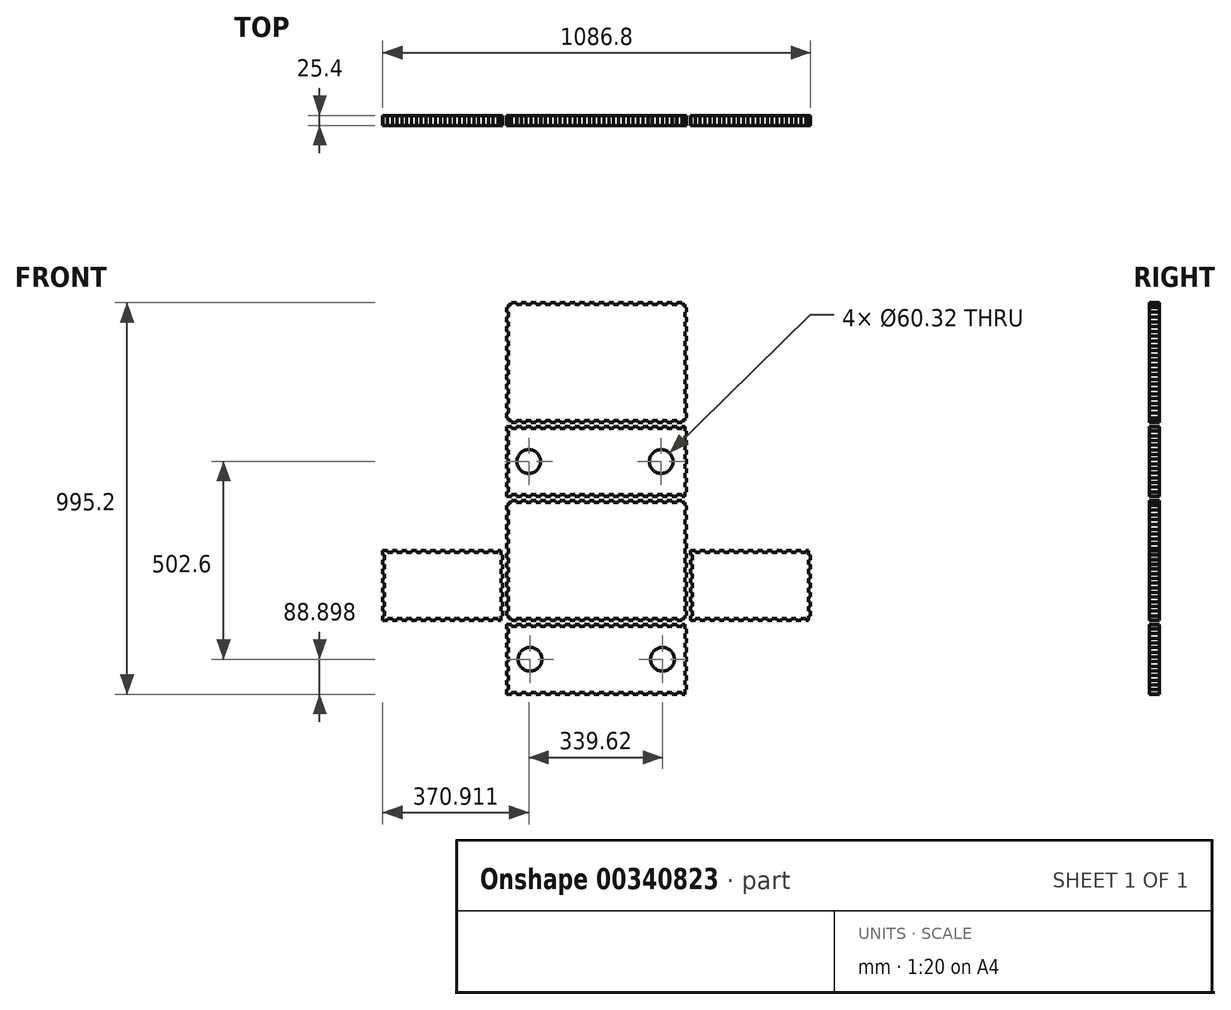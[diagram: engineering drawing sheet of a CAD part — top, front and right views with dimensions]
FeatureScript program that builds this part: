
annotation { "Feature Type Name" : "Feature", "Feature Type Description" : "" }
export const myFeature = defineFeature(function(context is Context, id is Id, definition is map)
    precondition{}
    {
        {
            var Q0;
            Q0=qCreatedBy(makeId("Front.planeOp"),FACE);
            var sketch = newSketch(context, id + "F0", { "sketchPlane" : qUnion([Q0])});
            skLineSegment(sketch, "E0", {"start": v(-228.6, -497.6) * mm, "end": v(-216.24, -497.6) * mm});
            skLineSegment(sketch, "E1", {"start": v(-216.24, -492.84) * mm, "end": v(-216.24, -497.6) * mm});
            skLineSegment(sketch, "E2", {"start": v(-216.24, -492.84) * mm, "end": v(-203.89, -492.84) * mm});
            skLineSegment(sketch, "E3", {"start": v(-203.89, -492.84) * mm, "end": v(-203.89, -497.6) * mm});
            skLineSegment(sketch, "E4", {"start": v(-203.89, -497.6) * mm, "end": v(-191.53, -497.6) * mm});
            skLineSegment(sketch, "E5", {"start": v(-191.53, -492.84) * mm, "end": v(-191.53, -497.6) * mm});
            skLineSegment(sketch, "E6", {"start": v(-191.53, -492.84) * mm, "end": v(-179.17, -492.84) * mm});
            skLineSegment(sketch, "E7", {"start": v(-179.17, -492.84) * mm, "end": v(-179.17, -497.6) * mm});
            skLineSegment(sketch, "E8", {"start": v(-179.17, -497.6) * mm, "end": v(-166.81, -497.6) * mm});
            skLineSegment(sketch, "E9", {"start": v(-166.81, -492.84) * mm, "end": v(-166.81, -497.6) * mm});
            skLineSegment(sketch, "E10", {"start": v(-166.81, -492.84) * mm, "end": v(-154.46, -492.84) * mm});
            skLineSegment(sketch, "E11", {"start": v(-154.46, -492.84) * mm, "end": v(-154.46, -497.6) * mm});
            skLineSegment(sketch, "E12", {"start": v(-154.46, -497.6) * mm, "end": v(-142.1, -497.6) * mm});
            skLineSegment(sketch, "E13", {"start": v(-142.1, -492.84) * mm, "end": v(-142.1, -497.6) * mm});
            skLineSegment(sketch, "E14", {"start": v(-142.1, -492.84) * mm, "end": v(-129.75, -492.84) * mm});
            skLineSegment(sketch, "E15", {"start": v(-129.75, -492.84) * mm, "end": v(-129.75, -497.6) * mm});
            skLineSegment(sketch, "E16", {"start": v(-129.75, -497.6) * mm, "end": v(-117.39, -497.6) * mm});
            skLineSegment(sketch, "E17", {"start": v(-117.39, -492.84) * mm, "end": v(-117.39, -497.6) * mm});
            skLineSegment(sketch, "E18", {"start": v(-117.39, -492.84) * mm, "end": v(-105.03, -492.84) * mm});
            skLineSegment(sketch, "E19", {"start": v(-105.03, -492.84) * mm, "end": v(-105.03, -497.6) * mm});
            skLineSegment(sketch, "E20", {"start": v(-105.03, -497.6) * mm, "end": v(-92.68, -497.6) * mm});
            skLineSegment(sketch, "E21", {"start": v(-92.68, -492.84) * mm, "end": v(-92.68, -497.6) * mm});
            skLineSegment(sketch, "E22", {"start": v(-92.68, -492.84) * mm, "end": v(-80.32, -492.84) * mm});
            skLineSegment(sketch, "E23", {"start": v(-80.32, -492.84) * mm, "end": v(-80.32, -497.6) * mm});
            skLineSegment(sketch, "E24", {"start": v(-80.32, -497.6) * mm, "end": v(-67.96, -497.6) * mm});
            skLineSegment(sketch, "E25", {"start": v(-67.96, -492.84) * mm, "end": v(-67.96, -497.6) * mm});
            skLineSegment(sketch, "E26", {"start": v(-67.96, -492.84) * mm, "end": v(-55.6, -492.84) * mm});
            skLineSegment(sketch, "E27", {"start": v(-55.6, -492.84) * mm, "end": v(-55.6, -497.6) * mm});
            skLineSegment(sketch, "E28", {"start": v(-55.6, -497.6) * mm, "end": v(-43.25, -497.6) * mm});
            skLineSegment(sketch, "E29", {"start": v(-43.25, -492.84) * mm, "end": v(-43.25, -497.6) * mm});
            skLineSegment(sketch, "E30", {"start": v(-43.25, -492.84) * mm, "end": v(-30.89, -492.84) * mm});
            skLineSegment(sketch, "E31", {"start": v(-30.89, -492.84) * mm, "end": v(-30.89, -497.6) * mm});
            skLineSegment(sketch, "E32", {"start": v(-30.89, -497.6) * mm, "end": v(-18.54, -497.6) * mm});
            skLineSegment(sketch, "E33", {"start": v(-18.54, -492.84) * mm, "end": v(-18.54, -497.6) * mm});
            skLineSegment(sketch, "E34", {"start": v(-18.54, -492.84) * mm, "end": v(-6.18, -492.84) * mm});
            skLineSegment(sketch, "E35", {"start": v(-6.18, -492.84) * mm, "end": v(-6.18, -497.6) * mm});
            skLineSegment(sketch, "E36", {"start": v(-6.18, -497.6) * mm, "end": v(6.18, -497.6) * mm});
            skLineSegment(sketch, "E37", {"start": v(6.18, -492.84) * mm, "end": v(6.18, -497.6) * mm});
            skLineSegment(sketch, "E38", {"start": v(6.18, -492.84) * mm, "end": v(18.53, -492.84) * mm});
            skLineSegment(sketch, "E39", {"start": v(18.53, -492.84) * mm, "end": v(18.53, -497.6) * mm});
            skLineSegment(sketch, "E40", {"start": v(18.53, -497.6) * mm, "end": v(30.9, -497.6) * mm});
            skLineSegment(sketch, "E41", {"start": v(30.9, -492.84) * mm, "end": v(30.9, -497.6) * mm});
            skLineSegment(sketch, "E42", {"start": v(30.9, -492.84) * mm, "end": v(43.25, -492.84) * mm});
            skLineSegment(sketch, "E43", {"start": v(43.25, -492.84) * mm, "end": v(43.25, -497.6) * mm});
            skLineSegment(sketch, "E44", {"start": v(43.25, -497.6) * mm, "end": v(55.6, -497.6) * mm});
            skLineSegment(sketch, "E45", {"start": v(55.6, -492.84) * mm, "end": v(55.6, -497.6) * mm});
            skLineSegment(sketch, "E46", {"start": v(55.6, -492.84) * mm, "end": v(67.96, -492.84) * mm});
            skLineSegment(sketch, "E47", {"start": v(67.96, -492.84) * mm, "end": v(67.96, -497.6) * mm});
            skLineSegment(sketch, "E48", {"start": v(67.96, -497.6) * mm, "end": v(80.32, -497.6) * mm});
            skLineSegment(sketch, "E49", {"start": v(80.32, -492.84) * mm, "end": v(80.32, -497.6) * mm});
            skLineSegment(sketch, "E50", {"start": v(80.32, -492.84) * mm, "end": v(92.67, -492.84) * mm});
            skLineSegment(sketch, "E51", {"start": v(92.67, -492.84) * mm, "end": v(92.67, -497.6) * mm});
            skLineSegment(sketch, "E52", {"start": v(92.67, -497.6) * mm, "end": v(105.03, -497.6) * mm});
            skLineSegment(sketch, "E53", {"start": v(105.03, -492.84) * mm, "end": v(105.03, -497.6) * mm});
            skLineSegment(sketch, "E54", {"start": v(105.03, -492.84) * mm, "end": v(117.39, -492.84) * mm});
            skLineSegment(sketch, "E55", {"start": v(117.39, -492.84) * mm, "end": v(117.39, -497.6) * mm});
            skLineSegment(sketch, "E56", {"start": v(117.39, -497.6) * mm, "end": v(129.75, -497.6) * mm});
            skLineSegment(sketch, "E57", {"start": v(129.75, -492.84) * mm, "end": v(129.75, -497.6) * mm});
            skLineSegment(sketch, "E58", {"start": v(129.75, -492.84) * mm, "end": v(142.1, -492.84) * mm});
            skLineSegment(sketch, "E59", {"start": v(142.1, -492.84) * mm, "end": v(142.1, -497.6) * mm});
            skLineSegment(sketch, "E60", {"start": v(142.1, -497.6) * mm, "end": v(154.46, -497.6) * mm});
            skLineSegment(sketch, "E61", {"start": v(154.46, -492.84) * mm, "end": v(154.46, -497.6) * mm});
            skLineSegment(sketch, "E62", {"start": v(154.46, -492.84) * mm, "end": v(166.82, -492.84) * mm});
            skLineSegment(sketch, "E63", {"start": v(166.82, -492.84) * mm, "end": v(166.82, -497.6) * mm});
            skLineSegment(sketch, "E64", {"start": v(166.82, -497.6) * mm, "end": v(179.17, -497.6) * mm});
            skLineSegment(sketch, "E65", {"start": v(179.17, -492.84) * mm, "end": v(179.17, -497.6) * mm});
            skLineSegment(sketch, "E66", {"start": v(179.17, -492.84) * mm, "end": v(191.53, -492.84) * mm});
            skLineSegment(sketch, "E67", {"start": v(191.53, -492.84) * mm, "end": v(191.53, -497.6) * mm});
            skLineSegment(sketch, "E68", {"start": v(191.53, -497.6) * mm, "end": v(203.89, -497.6) * mm});
            skLineSegment(sketch, "E69", {"start": v(203.89, -492.84) * mm, "end": v(203.89, -497.6) * mm});
            skLineSegment(sketch, "E70", {"start": v(203.89, -492.84) * mm, "end": v(216.25, -492.84) * mm});
            skLineSegment(sketch, "E71", {"start": v(216.25, -492.84) * mm, "end": v(216.25, -497.6) * mm});
            skLineSegment(sketch, "E72", {"start": v(216.25, -497.6) * mm, "end": v(223.84, -497.6) * mm});
            skLineSegment(sketch, "E73", {"start": v(-228.6, -319.8) * mm, "end": v(-216.24, -319.8) * mm});
            skLineSegment(sketch, "E74", {"start": v(-216.24, -319.8) * mm, "end": v(-216.24, -324.56) * mm});
            skLineSegment(sketch, "E75", {"start": v(-216.24, -324.56) * mm, "end": v(-203.89, -324.56) * mm});
            skLineSegment(sketch, "E76", {"start": v(-203.89, -319.8) * mm, "end": v(-203.89, -324.56) * mm});
            skLineSegment(sketch, "E77", {"start": v(-203.89, -319.8) * mm, "end": v(-191.53, -319.8) * mm});
            skLineSegment(sketch, "E78", {"start": v(-191.53, -319.8) * mm, "end": v(-191.53, -324.56) * mm});
            skLineSegment(sketch, "E79", {"start": v(-191.53, -324.56) * mm, "end": v(-179.17, -324.56) * mm});
            skLineSegment(sketch, "E80", {"start": v(-179.17, -319.8) * mm, "end": v(-179.17, -324.56) * mm});
            skLineSegment(sketch, "E81", {"start": v(-179.17, -319.8) * mm, "end": v(-166.81, -319.8) * mm});
            skLineSegment(sketch, "E82", {"start": v(-166.81, -319.8) * mm, "end": v(-166.81, -324.56) * mm});
            skLineSegment(sketch, "E83", {"start": v(-166.81, -324.56) * mm, "end": v(-154.46, -324.56) * mm});
            skLineSegment(sketch, "E84", {"start": v(-154.46, -319.8) * mm, "end": v(-154.46, -324.56) * mm});
            skLineSegment(sketch, "E85", {"start": v(-154.46, -319.8) * mm, "end": v(-142.1, -319.8) * mm});
            skLineSegment(sketch, "E86", {"start": v(-142.1, -319.8) * mm, "end": v(-142.1, -324.56) * mm});
            skLineSegment(sketch, "E87", {"start": v(-142.1, -324.56) * mm, "end": v(-129.75, -324.56) * mm});
            skLineSegment(sketch, "E88", {"start": v(-129.75, -319.8) * mm, "end": v(-129.75, -324.56) * mm});
            skLineSegment(sketch, "E89", {"start": v(-129.75, -319.8) * mm, "end": v(-117.39, -319.8) * mm});
            skLineSegment(sketch, "E90", {"start": v(-117.39, -319.8) * mm, "end": v(-117.39, -324.56) * mm});
            skLineSegment(sketch, "E91", {"start": v(-117.39, -324.56) * mm, "end": v(-105.03, -324.56) * mm});
            skLineSegment(sketch, "E92", {"start": v(-105.03, -319.8) * mm, "end": v(-105.03, -324.56) * mm});
            skLineSegment(sketch, "E93", {"start": v(-105.03, -319.8) * mm, "end": v(-92.68, -319.8) * mm});
            skLineSegment(sketch, "E94", {"start": v(-92.68, -319.8) * mm, "end": v(-92.68, -324.56) * mm});
            skLineSegment(sketch, "E95", {"start": v(-92.68, -324.56) * mm, "end": v(-80.32, -324.56) * mm});
            skLineSegment(sketch, "E96", {"start": v(-80.32, -319.8) * mm, "end": v(-80.32, -324.56) * mm});
            skLineSegment(sketch, "E97", {"start": v(-80.32, -319.8) * mm, "end": v(-67.96, -319.8) * mm});
            skLineSegment(sketch, "E98", {"start": v(-67.96, -319.8) * mm, "end": v(-67.96, -324.56) * mm});
            skLineSegment(sketch, "E99", {"start": v(-67.96, -324.56) * mm, "end": v(-55.6, -324.56) * mm});
            skLineSegment(sketch, "E100", {"start": v(-55.6, -319.8) * mm, "end": v(-55.6, -324.56) * mm});
            skLineSegment(sketch, "E101", {"start": v(-55.6, -319.8) * mm, "end": v(-43.25, -319.8) * mm});
            skLineSegment(sketch, "E102", {"start": v(-43.25, -319.8) * mm, "end": v(-43.25, -324.56) * mm});
            skLineSegment(sketch, "E103", {"start": v(-43.25, -324.56) * mm, "end": v(-30.89, -324.56) * mm});
            skLineSegment(sketch, "E104", {"start": v(-30.89, -319.8) * mm, "end": v(-30.89, -324.56) * mm});
            skLineSegment(sketch, "E105", {"start": v(-30.89, -319.8) * mm, "end": v(-18.54, -319.8) * mm});
            skLineSegment(sketch, "E106", {"start": v(-18.54, -319.8) * mm, "end": v(-18.54, -324.56) * mm});
            skLineSegment(sketch, "E107", {"start": v(-18.54, -324.56) * mm, "end": v(-6.18, -324.56) * mm});
            skLineSegment(sketch, "E108", {"start": v(-6.18, -319.8) * mm, "end": v(-6.18, -324.56) * mm});
            skLineSegment(sketch, "E109", {"start": v(-6.18, -319.8) * mm, "end": v(6.18, -319.8) * mm});
            skLineSegment(sketch, "E110", {"start": v(6.18, -319.8) * mm, "end": v(6.18, -324.56) * mm});
            skLineSegment(sketch, "E111", {"start": v(6.18, -324.56) * mm, "end": v(18.53, -324.56) * mm});
            skLineSegment(sketch, "E112", {"start": v(18.53, -319.8) * mm, "end": v(18.53, -324.56) * mm});
            skLineSegment(sketch, "E113", {"start": v(18.53, -319.8) * mm, "end": v(30.9, -319.8) * mm});
            skLineSegment(sketch, "E114", {"start": v(30.9, -319.8) * mm, "end": v(30.9, -324.56) * mm});
            skLineSegment(sketch, "E115", {"start": v(30.9, -324.56) * mm, "end": v(43.25, -324.56) * mm});
            skLineSegment(sketch, "E116", {"start": v(43.25, -319.8) * mm, "end": v(43.25, -324.56) * mm});
            skLineSegment(sketch, "E117", {"start": v(43.25, -319.8) * mm, "end": v(55.6, -319.8) * mm});
            skLineSegment(sketch, "E118", {"start": v(55.6, -319.8) * mm, "end": v(55.6, -324.56) * mm});
            skLineSegment(sketch, "E119", {"start": v(55.6, -324.56) * mm, "end": v(67.96, -324.56) * mm});
            skLineSegment(sketch, "E120", {"start": v(67.96, -319.8) * mm, "end": v(67.96, -324.56) * mm});
            skLineSegment(sketch, "E121", {"start": v(67.96, -319.8) * mm, "end": v(80.32, -319.8) * mm});
            skLineSegment(sketch, "E122", {"start": v(80.32, -319.8) * mm, "end": v(80.32, -324.56) * mm});
            skLineSegment(sketch, "E123", {"start": v(80.32, -324.56) * mm, "end": v(92.67, -324.56) * mm});
            skLineSegment(sketch, "E124", {"start": v(92.67, -319.8) * mm, "end": v(92.67, -324.56) * mm});
            skLineSegment(sketch, "E125", {"start": v(92.67, -319.8) * mm, "end": v(105.03, -319.8) * mm});
            skLineSegment(sketch, "E126", {"start": v(105.03, -319.8) * mm, "end": v(105.03, -324.56) * mm});
            skLineSegment(sketch, "E127", {"start": v(105.03, -324.56) * mm, "end": v(117.39, -324.56) * mm});
            skLineSegment(sketch, "E128", {"start": v(117.39, -319.8) * mm, "end": v(117.39, -324.56) * mm});
            skLineSegment(sketch, "E129", {"start": v(117.39, -319.8) * mm, "end": v(129.75, -319.8) * mm});
            skLineSegment(sketch, "E130", {"start": v(129.75, -319.8) * mm, "end": v(129.75, -324.56) * mm});
            skLineSegment(sketch, "E131", {"start": v(129.75, -324.56) * mm, "end": v(142.1, -324.56) * mm});
            skLineSegment(sketch, "E132", {"start": v(142.1, -319.8) * mm, "end": v(142.1, -324.56) * mm});
            skLineSegment(sketch, "E133", {"start": v(142.1, -319.8) * mm, "end": v(154.46, -319.8) * mm});
            skLineSegment(sketch, "E134", {"start": v(154.46, -319.8) * mm, "end": v(154.46, -324.56) * mm});
            skLineSegment(sketch, "E135", {"start": v(154.46, -324.56) * mm, "end": v(166.82, -324.56) * mm});
            skLineSegment(sketch, "E136", {"start": v(166.82, -319.8) * mm, "end": v(166.82, -324.56) * mm});
            skLineSegment(sketch, "E137", {"start": v(166.82, -319.8) * mm, "end": v(179.17, -319.8) * mm});
            skLineSegment(sketch, "E138", {"start": v(179.17, -319.8) * mm, "end": v(179.17, -324.56) * mm});
            skLineSegment(sketch, "E139", {"start": v(179.17, -324.56) * mm, "end": v(191.53, -324.56) * mm});
            skLineSegment(sketch, "E140", {"start": v(191.53, -319.8) * mm, "end": v(191.53, -324.56) * mm});
            skLineSegment(sketch, "E141", {"start": v(191.53, -319.8) * mm, "end": v(203.89, -319.8) * mm});
            skLineSegment(sketch, "E142", {"start": v(203.89, -319.8) * mm, "end": v(203.89, -324.56) * mm});
            skLineSegment(sketch, "E143", {"start": v(203.89, -324.56) * mm, "end": v(216.25, -324.56) * mm});
            skLineSegment(sketch, "E144", {"start": v(216.25, -319.8) * mm, "end": v(216.25, -324.56) * mm});
            skLineSegment(sketch, "E145", {"start": v(216.25, -319.8) * mm, "end": v(223.84, -319.8) * mm});
            skLineSegment(sketch, "E146", {"start": v(-228.6, -497.6) * mm, "end": v(-228.6, -485.75) * mm});
            skLineSegment(sketch, "E147", {"start": v(-223.84, -485.75) * mm, "end": v(-228.6, -485.75) * mm});
            skLineSegment(sketch, "E148", {"start": v(-223.84, -485.75) * mm, "end": v(-223.84, -473.9) * mm});
            skLineSegment(sketch, "E149", {"start": v(-223.84, -473.9) * mm, "end": v(-228.6, -473.9) * mm});
            skLineSegment(sketch, "E150", {"start": v(-228.6, -473.9) * mm, "end": v(-228.6, -462.04) * mm});
            skLineSegment(sketch, "E151", {"start": v(-223.84, -462.04) * mm, "end": v(-228.6, -462.04) * mm});
            skLineSegment(sketch, "E152", {"start": v(-223.84, -462.04) * mm, "end": v(-223.84, -450.19) * mm});
            skLineSegment(sketch, "E153", {"start": v(-223.84, -450.19) * mm, "end": v(-228.6, -450.19) * mm});
            skLineSegment(sketch, "E154", {"start": v(-228.6, -450.19) * mm, "end": v(-228.6, -438.33) * mm});
            skLineSegment(sketch, "E155", {"start": v(-223.84, -438.33) * mm, "end": v(-228.6, -438.33) * mm});
            skLineSegment(sketch, "E156", {"start": v(-223.84, -438.33) * mm, "end": v(-223.84, -426.48) * mm});
            skLineSegment(sketch, "E157", {"start": v(-223.84, -426.48) * mm, "end": v(-228.6, -426.48) * mm});
            skLineSegment(sketch, "E158", {"start": v(-228.6, -426.48) * mm, "end": v(-228.6, -414.63) * mm});
            skLineSegment(sketch, "E159", {"start": v(-223.84, -414.63) * mm, "end": v(-228.6, -414.63) * mm});
            skLineSegment(sketch, "E160", {"start": v(-223.84, -414.63) * mm, "end": v(-223.84, -402.78) * mm});
            skLineSegment(sketch, "E161", {"start": v(-223.84, -402.78) * mm, "end": v(-228.6, -402.78) * mm});
            skLineSegment(sketch, "E162", {"start": v(-228.6, -402.78) * mm, "end": v(-228.6, -390.92) * mm});
            skLineSegment(sketch, "E163", {"start": v(-223.84, -390.92) * mm, "end": v(-228.6, -390.92) * mm});
            skLineSegment(sketch, "E164", {"start": v(-223.84, -390.92) * mm, "end": v(-223.84, -379.07) * mm});
            skLineSegment(sketch, "E165", {"start": v(-223.84, -379.07) * mm, "end": v(-228.6, -379.07) * mm});
            skLineSegment(sketch, "E166", {"start": v(-228.6, -379.07) * mm, "end": v(-228.6, -367.22) * mm});
            skLineSegment(sketch, "E167", {"start": v(-223.84, -367.22) * mm, "end": v(-228.6, -367.22) * mm});
            skLineSegment(sketch, "E168", {"start": v(-223.84, -367.22) * mm, "end": v(-223.84, -355.36) * mm});
            skLineSegment(sketch, "E169", {"start": v(-223.84, -355.36) * mm, "end": v(-228.6, -355.36) * mm});
            skLineSegment(sketch, "E170", {"start": v(-228.6, -355.36) * mm, "end": v(-228.6, -343.5) * mm});
            skLineSegment(sketch, "E171", {"start": v(-223.84, -343.5) * mm, "end": v(-228.6, -343.5) * mm});
            skLineSegment(sketch, "E172", {"start": v(-223.84, -343.5) * mm, "end": v(-223.84, -331.65) * mm});
            skLineSegment(sketch, "E173", {"start": v(-223.84, -331.65) * mm, "end": v(-228.6, -331.65) * mm});
            skLineSegment(sketch, "E174", {"start": v(-228.6, -331.65) * mm, "end": v(-228.6, -319.8) * mm});
            skLineSegment(sketch, "E175", {"start": v(223.84, -497.6) * mm, "end": v(223.84, -485.75) * mm});
            skLineSegment(sketch, "E176", {"start": v(228.6, -485.75) * mm, "end": v(223.84, -485.75) * mm});
            skLineSegment(sketch, "E177", {"start": v(228.6, -485.75) * mm, "end": v(228.6, -473.9) * mm});
            skLineSegment(sketch, "E178", {"start": v(228.6, -473.9) * mm, "end": v(223.84, -473.9) * mm});
            skLineSegment(sketch, "E179", {"start": v(223.84, -473.9) * mm, "end": v(223.84, -462.04) * mm});
            skLineSegment(sketch, "E180", {"start": v(228.6, -462.04) * mm, "end": v(223.84, -462.04) * mm});
            skLineSegment(sketch, "E181", {"start": v(228.6, -462.04) * mm, "end": v(228.6, -450.19) * mm});
            skLineSegment(sketch, "E182", {"start": v(228.6, -450.19) * mm, "end": v(223.84, -450.19) * mm});
            skLineSegment(sketch, "E183", {"start": v(223.84, -450.19) * mm, "end": v(223.84, -438.33) * mm});
            skLineSegment(sketch, "E184", {"start": v(228.6, -438.33) * mm, "end": v(223.84, -438.33) * mm});
            skLineSegment(sketch, "E185", {"start": v(228.6, -438.33) * mm, "end": v(228.6, -426.48) * mm});
            skLineSegment(sketch, "E186", {"start": v(228.6, -426.48) * mm, "end": v(223.84, -426.48) * mm});
            skLineSegment(sketch, "E187", {"start": v(223.84, -426.48) * mm, "end": v(223.84, -414.63) * mm});
            skLineSegment(sketch, "E188", {"start": v(228.6, -414.63) * mm, "end": v(223.84, -414.63) * mm});
            skLineSegment(sketch, "E189", {"start": v(228.6, -414.63) * mm, "end": v(228.6, -402.78) * mm});
            skLineSegment(sketch, "E190", {"start": v(228.6, -402.78) * mm, "end": v(223.84, -402.78) * mm});
            skLineSegment(sketch, "E191", {"start": v(223.84, -402.78) * mm, "end": v(223.84, -390.92) * mm});
            skLineSegment(sketch, "E192", {"start": v(228.6, -390.92) * mm, "end": v(223.84, -390.92) * mm});
            skLineSegment(sketch, "E193", {"start": v(228.6, -390.92) * mm, "end": v(228.6, -379.07) * mm});
            skLineSegment(sketch, "E194", {"start": v(228.6, -379.07) * mm, "end": v(223.84, -379.07) * mm});
            skLineSegment(sketch, "E195", {"start": v(223.84, -379.07) * mm, "end": v(223.84, -367.22) * mm});
            skLineSegment(sketch, "E196", {"start": v(228.6, -367.22) * mm, "end": v(223.84, -367.22) * mm});
            skLineSegment(sketch, "E197", {"start": v(228.6, -367.22) * mm, "end": v(228.6, -355.36) * mm});
            skLineSegment(sketch, "E198", {"start": v(228.6, -355.36) * mm, "end": v(223.84, -355.36) * mm});
            skLineSegment(sketch, "E199", {"start": v(223.84, -355.36) * mm, "end": v(223.84, -343.5) * mm});
            skLineSegment(sketch, "E200", {"start": v(228.6, -343.5) * mm, "end": v(223.84, -343.5) * mm});
            skLineSegment(sketch, "E201", {"start": v(228.6, -343.5) * mm, "end": v(228.6, -331.65) * mm});
            skLineSegment(sketch, "E202", {"start": v(228.6, -331.65) * mm, "end": v(223.84, -331.65) * mm});
            skLineSegment(sketch, "E203", {"start": v(223.84, -331.65) * mm, "end": v(223.84, -319.8) * mm});
            skLineSegment(sketch, "E204", {"start": v(-543.4, -309.8) * mm, "end": v(-531.2, -309.8) * mm});
            skLineSegment(sketch, "E205", {"start": v(-531.2, -305.04) * mm, "end": v(-531.2, -309.8) * mm});
            skLineSegment(sketch, "E206", {"start": v(-531.2, -305.04) * mm, "end": v(-519.02, -305.04) * mm});
            skLineSegment(sketch, "E207", {"start": v(-519.02, -305.04) * mm, "end": v(-519.02, -309.8) * mm});
            skLineSegment(sketch, "E208", {"start": v(-519.02, -309.8) * mm, "end": v(-506.82, -309.8) * mm});
            skLineSegment(sketch, "E209", {"start": v(-506.82, -305.04) * mm, "end": v(-506.82, -309.8) * mm});
            skLineSegment(sketch, "E210", {"start": v(-506.82, -305.04) * mm, "end": v(-494.63, -305.04) * mm});
            skLineSegment(sketch, "E211", {"start": v(-494.63, -305.04) * mm, "end": v(-494.63, -309.8) * mm});
            skLineSegment(sketch, "E212", {"start": v(-494.63, -309.8) * mm, "end": v(-482.44, -309.8) * mm});
            skLineSegment(sketch, "E213", {"start": v(-482.44, -305.04) * mm, "end": v(-482.44, -309.8) * mm});
            skLineSegment(sketch, "E214", {"start": v(-482.44, -305.04) * mm, "end": v(-470.25, -305.04) * mm});
            skLineSegment(sketch, "E215", {"start": v(-470.25, -305.04) * mm, "end": v(-470.25, -309.8) * mm});
            skLineSegment(sketch, "E216", {"start": v(-470.25, -309.8) * mm, "end": v(-458.06, -309.8) * mm});
            skLineSegment(sketch, "E217", {"start": v(-458.06, -305.04) * mm, "end": v(-458.06, -309.8) * mm});
            skLineSegment(sketch, "E218", {"start": v(-458.06, -305.04) * mm, "end": v(-445.86, -305.04) * mm});
            skLineSegment(sketch, "E219", {"start": v(-445.86, -305.04) * mm, "end": v(-445.86, -309.8) * mm});
            skLineSegment(sketch, "E220", {"start": v(-445.86, -309.8) * mm, "end": v(-433.67, -309.8) * mm});
            skLineSegment(sketch, "E221", {"start": v(-433.67, -305.04) * mm, "end": v(-433.67, -309.8) * mm});
            skLineSegment(sketch, "E222", {"start": v(-433.67, -305.04) * mm, "end": v(-421.48, -305.04) * mm});
            skLineSegment(sketch, "E223", {"start": v(-421.48, -305.04) * mm, "end": v(-421.48, -309.8) * mm});
            skLineSegment(sketch, "E224", {"start": v(-421.48, -309.8) * mm, "end": v(-409.29, -309.8) * mm});
            skLineSegment(sketch, "E225", {"start": v(-409.29, -305.04) * mm, "end": v(-409.29, -309.8) * mm});
            skLineSegment(sketch, "E226", {"start": v(-409.29, -305.04) * mm, "end": v(-397.1, -305.04) * mm});
            skLineSegment(sketch, "E227", {"start": v(-397.1, -305.04) * mm, "end": v(-397.1, -309.8) * mm});
            skLineSegment(sketch, "E228", {"start": v(-397.1, -309.8) * mm, "end": v(-384.9, -309.8) * mm});
            skLineSegment(sketch, "E229", {"start": v(-384.9, -305.04) * mm, "end": v(-384.9, -309.8) * mm});
            skLineSegment(sketch, "E230", {"start": v(-384.9, -305.04) * mm, "end": v(-372.71, -305.04) * mm});
            skLineSegment(sketch, "E231", {"start": v(-372.71, -305.04) * mm, "end": v(-372.71, -309.8) * mm});
            skLineSegment(sketch, "E232", {"start": v(-372.71, -309.8) * mm, "end": v(-360.52, -309.8) * mm});
            skLineSegment(sketch, "E233", {"start": v(-360.52, -305.04) * mm, "end": v(-360.52, -309.8) * mm});
            skLineSegment(sketch, "E234", {"start": v(-360.52, -305.04) * mm, "end": v(-348.33, -305.04) * mm});
            skLineSegment(sketch, "E235", {"start": v(-348.33, -305.04) * mm, "end": v(-348.33, -309.8) * mm});
            skLineSegment(sketch, "E236", {"start": v(-348.33, -309.8) * mm, "end": v(-336.14, -309.8) * mm});
            skLineSegment(sketch, "E237", {"start": v(-336.14, -305.04) * mm, "end": v(-336.14, -309.8) * mm});
            skLineSegment(sketch, "E238", {"start": v(-336.14, -305.04) * mm, "end": v(-323.94, -305.04) * mm});
            skLineSegment(sketch, "E239", {"start": v(-323.94, -305.04) * mm, "end": v(-323.94, -309.8) * mm});
            skLineSegment(sketch, "E240", {"start": v(-323.94, -309.8) * mm, "end": v(-311.75, -309.8) * mm});
            skLineSegment(sketch, "E241", {"start": v(-311.75, -305.04) * mm, "end": v(-311.75, -309.8) * mm});
            skLineSegment(sketch, "E242", {"start": v(-311.75, -305.04) * mm, "end": v(-299.56, -305.04) * mm});
            skLineSegment(sketch, "E243", {"start": v(-299.56, -305.04) * mm, "end": v(-299.56, -309.8) * mm});
            skLineSegment(sketch, "E244", {"start": v(-299.56, -309.8) * mm, "end": v(-287.37, -309.8) * mm});
            skLineSegment(sketch, "E245", {"start": v(-287.37, -305.04) * mm, "end": v(-287.37, -309.8) * mm});
            skLineSegment(sketch, "E246", {"start": v(-287.37, -305.04) * mm, "end": v(-275.18, -305.04) * mm});
            skLineSegment(sketch, "E247", {"start": v(-275.18, -305.04) * mm, "end": v(-275.18, -309.8) * mm});
            skLineSegment(sketch, "E248", {"start": v(-275.18, -309.8) * mm, "end": v(-262.98, -309.8) * mm});
            skLineSegment(sketch, "E249", {"start": v(-262.98, -305.04) * mm, "end": v(-262.98, -309.8) * mm});
            skLineSegment(sketch, "E250", {"start": v(-262.98, -305.04) * mm, "end": v(-250.8, -305.04) * mm});
            skLineSegment(sketch, "E251", {"start": v(-250.8, -305.04) * mm, "end": v(-250.8, -309.8) * mm});
            skLineSegment(sketch, "E252", {"start": v(-250.8, -309.8) * mm, "end": v(-243.36, -309.8) * mm});
            skLineSegment(sketch, "E253", {"start": v(-543.4, -132) * mm, "end": v(-531.2, -132) * mm});
            skLineSegment(sketch, "E254", {"start": v(-531.2, -132) * mm, "end": v(-531.2, -136.76) * mm});
            skLineSegment(sketch, "E255", {"start": v(-531.2, -136.76) * mm, "end": v(-519.02, -136.76) * mm});
            skLineSegment(sketch, "E256", {"start": v(-519.02, -132) * mm, "end": v(-519.02, -136.76) * mm});
            skLineSegment(sketch, "E257", {"start": v(-519.02, -132) * mm, "end": v(-506.82, -132) * mm});
            skLineSegment(sketch, "E258", {"start": v(-506.82, -132) * mm, "end": v(-506.82, -136.76) * mm});
            skLineSegment(sketch, "E259", {"start": v(-506.82, -136.76) * mm, "end": v(-494.63, -136.76) * mm});
            skLineSegment(sketch, "E260", {"start": v(-494.63, -132) * mm, "end": v(-494.63, -136.76) * mm});
            skLineSegment(sketch, "E261", {"start": v(-494.63, -132) * mm, "end": v(-482.44, -132) * mm});
            skLineSegment(sketch, "E262", {"start": v(-482.44, -132) * mm, "end": v(-482.44, -136.76) * mm});
            skLineSegment(sketch, "E263", {"start": v(-482.44, -136.76) * mm, "end": v(-470.25, -136.76) * mm});
            skLineSegment(sketch, "E264", {"start": v(-470.25, -132) * mm, "end": v(-470.25, -136.76) * mm});
            skLineSegment(sketch, "E265", {"start": v(-470.25, -132) * mm, "end": v(-458.06, -132) * mm});
            skLineSegment(sketch, "E266", {"start": v(-458.06, -132) * mm, "end": v(-458.06, -136.76) * mm});
            skLineSegment(sketch, "E267", {"start": v(-458.06, -136.76) * mm, "end": v(-445.86, -136.76) * mm});
            skLineSegment(sketch, "E268", {"start": v(-445.86, -132) * mm, "end": v(-445.86, -136.76) * mm});
            skLineSegment(sketch, "E269", {"start": v(-445.86, -132) * mm, "end": v(-433.67, -132) * mm});
            skLineSegment(sketch, "E270", {"start": v(-433.67, -132) * mm, "end": v(-433.67, -136.76) * mm});
            skLineSegment(sketch, "E271", {"start": v(-433.67, -136.76) * mm, "end": v(-421.48, -136.76) * mm});
            skLineSegment(sketch, "E272", {"start": v(-421.48, -132) * mm, "end": v(-421.48, -136.76) * mm});
            skLineSegment(sketch, "E273", {"start": v(-421.48, -132) * mm, "end": v(-409.29, -132) * mm});
            skLineSegment(sketch, "E274", {"start": v(-409.29, -132) * mm, "end": v(-409.29, -136.76) * mm});
            skLineSegment(sketch, "E275", {"start": v(-409.29, -136.76) * mm, "end": v(-397.1, -136.76) * mm});
            skLineSegment(sketch, "E276", {"start": v(-397.1, -132) * mm, "end": v(-397.1, -136.76) * mm});
            skLineSegment(sketch, "E277", {"start": v(-397.1, -132) * mm, "end": v(-384.9, -132) * mm});
            skLineSegment(sketch, "E278", {"start": v(-384.9, -132) * mm, "end": v(-384.9, -136.76) * mm});
            skLineSegment(sketch, "E279", {"start": v(-384.9, -136.76) * mm, "end": v(-372.71, -136.76) * mm});
            skLineSegment(sketch, "E280", {"start": v(-372.71, -132) * mm, "end": v(-372.71, -136.76) * mm});
            skLineSegment(sketch, "E281", {"start": v(-372.71, -132) * mm, "end": v(-360.52, -132) * mm});
            skLineSegment(sketch, "E282", {"start": v(-360.52, -132) * mm, "end": v(-360.52, -136.76) * mm});
            skLineSegment(sketch, "E283", {"start": v(-360.52, -136.76) * mm, "end": v(-348.33, -136.76) * mm});
            skLineSegment(sketch, "E284", {"start": v(-348.33, -132) * mm, "end": v(-348.33, -136.76) * mm});
            skLineSegment(sketch, "E285", {"start": v(-348.33, -132) * mm, "end": v(-336.14, -132) * mm});
            skLineSegment(sketch, "E286", {"start": v(-336.14, -132) * mm, "end": v(-336.14, -136.76) * mm});
            skLineSegment(sketch, "E287", {"start": v(-336.14, -136.76) * mm, "end": v(-323.94, -136.76) * mm});
            skLineSegment(sketch, "E288", {"start": v(-323.94, -132) * mm, "end": v(-323.94, -136.76) * mm});
            skLineSegment(sketch, "E289", {"start": v(-323.94, -132) * mm, "end": v(-311.75, -132) * mm});
            skLineSegment(sketch, "E290", {"start": v(-311.75, -132) * mm, "end": v(-311.75, -136.76) * mm});
            skLineSegment(sketch, "E291", {"start": v(-311.75, -136.76) * mm, "end": v(-299.56, -136.76) * mm});
            skLineSegment(sketch, "E292", {"start": v(-299.56, -132) * mm, "end": v(-299.56, -136.76) * mm});
            skLineSegment(sketch, "E293", {"start": v(-299.56, -132) * mm, "end": v(-287.37, -132) * mm});
            skLineSegment(sketch, "E294", {"start": v(-287.37, -132) * mm, "end": v(-287.37, -136.76) * mm});
            skLineSegment(sketch, "E295", {"start": v(-287.37, -136.76) * mm, "end": v(-275.18, -136.76) * mm});
            skLineSegment(sketch, "E296", {"start": v(-275.18, -132) * mm, "end": v(-275.18, -136.76) * mm});
            skLineSegment(sketch, "E297", {"start": v(-275.18, -132) * mm, "end": v(-262.98, -132) * mm});
            skLineSegment(sketch, "E298", {"start": v(-262.98, -132) * mm, "end": v(-262.98, -136.76) * mm});
            skLineSegment(sketch, "E299", {"start": v(-262.98, -136.76) * mm, "end": v(-250.8, -136.76) * mm});
            skLineSegment(sketch, "E300", {"start": v(-250.8, -132) * mm, "end": v(-250.8, -136.76) * mm});
            skLineSegment(sketch, "E301", {"start": v(-250.8, -132) * mm, "end": v(-243.36, -132) * mm});
            skLineSegment(sketch, "E302", {"start": v(-543.4, -309.8) * mm, "end": v(-543.4, -297.95) * mm});
            skLineSegment(sketch, "E303", {"start": v(-538.64, -297.95) * mm, "end": v(-543.4, -297.95) * mm});
            skLineSegment(sketch, "E304", {"start": v(-538.64, -297.95) * mm, "end": v(-538.64, -286.1) * mm});
            skLineSegment(sketch, "E305", {"start": v(-538.64, -286.1) * mm, "end": v(-543.4, -286.1) * mm});
            skLineSegment(sketch, "E306", {"start": v(-543.4, -286.1) * mm, "end": v(-543.4, -274.24) * mm});
            skLineSegment(sketch, "E307", {"start": v(-538.64, -274.24) * mm, "end": v(-543.4, -274.24) * mm});
            skLineSegment(sketch, "E308", {"start": v(-538.64, -274.24) * mm, "end": v(-538.64, -262.39) * mm});
            skLineSegment(sketch, "E309", {"start": v(-538.64, -262.39) * mm, "end": v(-543.4, -262.39) * mm});
            skLineSegment(sketch, "E310", {"start": v(-543.4, -262.39) * mm, "end": v(-543.4, -250.54) * mm});
            skLineSegment(sketch, "E311", {"start": v(-538.64, -250.54) * mm, "end": v(-543.4, -250.54) * mm});
            skLineSegment(sketch, "E312", {"start": v(-538.64, -250.54) * mm, "end": v(-538.64, -238.68) * mm});
            skLineSegment(sketch, "E313", {"start": v(-538.64, -238.68) * mm, "end": v(-543.4, -238.68) * mm});
            skLineSegment(sketch, "E314", {"start": v(-543.4, -238.68) * mm, "end": v(-543.4, -226.83) * mm});
            skLineSegment(sketch, "E315", {"start": v(-538.64, -226.83) * mm, "end": v(-543.4, -226.83) * mm});
            skLineSegment(sketch, "E316", {"start": v(-538.64, -226.83) * mm, "end": v(-538.64, -214.98) * mm});
            skLineSegment(sketch, "E317", {"start": v(-538.64, -214.98) * mm, "end": v(-543.4, -214.98) * mm});
            skLineSegment(sketch, "E318", {"start": v(-543.4, -214.98) * mm, "end": v(-543.4, -203.12) * mm});
            skLineSegment(sketch, "E319", {"start": v(-538.64, -203.12) * mm, "end": v(-543.4, -203.12) * mm});
            skLineSegment(sketch, "E320", {"start": v(-538.64, -203.12) * mm, "end": v(-538.64, -191.27) * mm});
            skLineSegment(sketch, "E321", {"start": v(-538.64, -191.27) * mm, "end": v(-543.4, -191.27) * mm});
            skLineSegment(sketch, "E322", {"start": v(-543.4, -191.27) * mm, "end": v(-543.4, -179.42) * mm});
            skLineSegment(sketch, "E323", {"start": v(-538.64, -179.42) * mm, "end": v(-543.4, -179.42) * mm});
            skLineSegment(sketch, "E324", {"start": v(-538.64, -179.42) * mm, "end": v(-538.64, -167.56) * mm});
            skLineSegment(sketch, "E325", {"start": v(-538.64, -167.56) * mm, "end": v(-543.4, -167.56) * mm});
            skLineSegment(sketch, "E326", {"start": v(-543.4, -167.56) * mm, "end": v(-543.4, -155.7) * mm});
            skLineSegment(sketch, "E327", {"start": v(-538.64, -155.7) * mm, "end": v(-543.4, -155.7) * mm});
            skLineSegment(sketch, "E328", {"start": v(-538.64, -155.7) * mm, "end": v(-538.64, -143.86) * mm});
            skLineSegment(sketch, "E329", {"start": v(-538.64, -143.86) * mm, "end": v(-543.4, -143.86) * mm});
            skLineSegment(sketch, "E330", {"start": v(-543.4, -143.86) * mm, "end": v(-543.4, -132) * mm});
            skLineSegment(sketch, "E331", {"start": v(-243.36, -309.8) * mm, "end": v(-243.36, -297.95) * mm});
            skLineSegment(sketch, "E332", {"start": v(-238.6, -297.95) * mm, "end": v(-243.36, -297.95) * mm});
            skLineSegment(sketch, "E333", {"start": v(-238.6, -297.95) * mm, "end": v(-238.6, -286.1) * mm});
            skLineSegment(sketch, "E334", {"start": v(-238.6, -286.1) * mm, "end": v(-243.36, -286.1) * mm});
            skLineSegment(sketch, "E335", {"start": v(-243.36, -286.1) * mm, "end": v(-243.36, -274.24) * mm});
            skLineSegment(sketch, "E336", {"start": v(-238.6, -274.24) * mm, "end": v(-243.36, -274.24) * mm});
            skLineSegment(sketch, "E337", {"start": v(-238.6, -274.24) * mm, "end": v(-238.6, -262.39) * mm});
            skLineSegment(sketch, "E338", {"start": v(-238.6, -262.39) * mm, "end": v(-243.36, -262.39) * mm});
            skLineSegment(sketch, "E339", {"start": v(-243.36, -262.39) * mm, "end": v(-243.36, -250.54) * mm});
            skLineSegment(sketch, "E340", {"start": v(-238.6, -250.54) * mm, "end": v(-243.36, -250.54) * mm});
            skLineSegment(sketch, "E341", {"start": v(-238.6, -250.54) * mm, "end": v(-238.6, -238.68) * mm});
            skLineSegment(sketch, "E342", {"start": v(-238.6, -238.68) * mm, "end": v(-243.36, -238.68) * mm});
            skLineSegment(sketch, "E343", {"start": v(-243.36, -238.68) * mm, "end": v(-243.36, -226.83) * mm});
            skLineSegment(sketch, "E344", {"start": v(-238.6, -226.83) * mm, "end": v(-243.36, -226.83) * mm});
            skLineSegment(sketch, "E345", {"start": v(-238.6, -226.83) * mm, "end": v(-238.6, -214.98) * mm});
            skLineSegment(sketch, "E346", {"start": v(-238.6, -214.98) * mm, "end": v(-243.36, -214.98) * mm});
            skLineSegment(sketch, "E347", {"start": v(-243.36, -214.98) * mm, "end": v(-243.36, -203.12) * mm});
            skLineSegment(sketch, "E348", {"start": v(-238.6, -203.12) * mm, "end": v(-243.36, -203.12) * mm});
            skLineSegment(sketch, "E349", {"start": v(-238.6, -203.12) * mm, "end": v(-238.6, -191.27) * mm});
            skLineSegment(sketch, "E350", {"start": v(-238.6, -191.27) * mm, "end": v(-243.36, -191.27) * mm});
            skLineSegment(sketch, "E351", {"start": v(-243.36, -191.27) * mm, "end": v(-243.36, -179.42) * mm});
            skLineSegment(sketch, "E352", {"start": v(-238.6, -179.42) * mm, "end": v(-243.36, -179.42) * mm});
            skLineSegment(sketch, "E353", {"start": v(-238.6, -179.42) * mm, "end": v(-238.6, -167.56) * mm});
            skLineSegment(sketch, "E354", {"start": v(-238.6, -167.56) * mm, "end": v(-243.36, -167.56) * mm});
            skLineSegment(sketch, "E355", {"start": v(-243.36, -167.56) * mm, "end": v(-243.36, -155.7) * mm});
            skLineSegment(sketch, "E356", {"start": v(-238.6, -155.7) * mm, "end": v(-243.36, -155.7) * mm});
            skLineSegment(sketch, "E357", {"start": v(-238.6, -155.7) * mm, "end": v(-238.6, -143.86) * mm});
            skLineSegment(sketch, "E358", {"start": v(-238.6, -143.86) * mm, "end": v(-243.36, -143.86) * mm});
            skLineSegment(sketch, "E359", {"start": v(-243.36, -143.86) * mm, "end": v(-243.36, -132) * mm});
            skLineSegment(sketch, "E360", {"start": v(-223.84, -305.04) * mm, "end": v(-216.24, -305.04) * mm});
            skLineSegment(sketch, "E361", {"start": v(-216.24, -305.04) * mm, "end": v(-216.24, -309.8) * mm});
            skLineSegment(sketch, "E362", {"start": v(-216.24, -309.8) * mm, "end": v(-203.89, -309.8) * mm});
            skLineSegment(sketch, "E363", {"start": v(-203.89, -305.04) * mm, "end": v(-203.89, -309.8) * mm});
            skLineSegment(sketch, "E364", {"start": v(-203.89, -305.04) * mm, "end": v(-191.53, -305.04) * mm});
            skLineSegment(sketch, "E365", {"start": v(-191.53, -305.04) * mm, "end": v(-191.53, -309.8) * mm});
            skLineSegment(sketch, "E366", {"start": v(-191.53, -309.8) * mm, "end": v(-179.17, -309.8) * mm});
            skLineSegment(sketch, "E367", {"start": v(-179.17, -305.04) * mm, "end": v(-179.17, -309.8) * mm});
            skLineSegment(sketch, "E368", {"start": v(-179.17, -305.04) * mm, "end": v(-166.81, -305.04) * mm});
            skLineSegment(sketch, "E369", {"start": v(-166.81, -305.04) * mm, "end": v(-166.81, -309.8) * mm});
            skLineSegment(sketch, "E370", {"start": v(-166.81, -309.8) * mm, "end": v(-154.46, -309.8) * mm});
            skLineSegment(sketch, "E371", {"start": v(-154.46, -305.04) * mm, "end": v(-154.46, -309.8) * mm});
            skLineSegment(sketch, "E372", {"start": v(-154.46, -305.04) * mm, "end": v(-142.1, -305.04) * mm});
            skLineSegment(sketch, "E373", {"start": v(-142.1, -305.04) * mm, "end": v(-142.1, -309.8) * mm});
            skLineSegment(sketch, "E374", {"start": v(-142.1, -309.8) * mm, "end": v(-129.75, -309.8) * mm});
            skLineSegment(sketch, "E375", {"start": v(-129.75, -305.04) * mm, "end": v(-129.75, -309.8) * mm});
            skLineSegment(sketch, "E376", {"start": v(-129.75, -305.04) * mm, "end": v(-117.39, -305.04) * mm});
            skLineSegment(sketch, "E377", {"start": v(-117.39, -305.04) * mm, "end": v(-117.39, -309.8) * mm});
            skLineSegment(sketch, "E378", {"start": v(-117.39, -309.8) * mm, "end": v(-105.03, -309.8) * mm});
            skLineSegment(sketch, "E379", {"start": v(-105.03, -305.04) * mm, "end": v(-105.03, -309.8) * mm});
            skLineSegment(sketch, "E380", {"start": v(-105.03, -305.04) * mm, "end": v(-92.68, -305.04) * mm});
            skLineSegment(sketch, "E381", {"start": v(-92.68, -305.04) * mm, "end": v(-92.68, -309.8) * mm});
            skLineSegment(sketch, "E382", {"start": v(-92.68, -309.8) * mm, "end": v(-80.32, -309.8) * mm});
            skLineSegment(sketch, "E383", {"start": v(-80.32, -305.04) * mm, "end": v(-80.32, -309.8) * mm});
            skLineSegment(sketch, "E384", {"start": v(-80.32, -305.04) * mm, "end": v(-67.96, -305.04) * mm});
            skLineSegment(sketch, "E385", {"start": v(-67.96, -305.04) * mm, "end": v(-67.96, -309.8) * mm});
            skLineSegment(sketch, "E386", {"start": v(-67.96, -309.8) * mm, "end": v(-55.6, -309.8) * mm});
            skLineSegment(sketch, "E387", {"start": v(-55.6, -305.04) * mm, "end": v(-55.6, -309.8) * mm});
            skLineSegment(sketch, "E388", {"start": v(-55.6, -305.04) * mm, "end": v(-43.25, -305.04) * mm});
            skLineSegment(sketch, "E389", {"start": v(-43.25, -305.04) * mm, "end": v(-43.25, -309.8) * mm});
            skLineSegment(sketch, "E390", {"start": v(-43.25, -309.8) * mm, "end": v(-30.89, -309.8) * mm});
            skLineSegment(sketch, "E391", {"start": v(-30.89, -305.04) * mm, "end": v(-30.89, -309.8) * mm});
            skLineSegment(sketch, "E392", {"start": v(-30.89, -305.04) * mm, "end": v(-18.54, -305.04) * mm});
            skLineSegment(sketch, "E393", {"start": v(-18.54, -305.04) * mm, "end": v(-18.54, -309.8) * mm});
            skLineSegment(sketch, "E394", {"start": v(-18.54, -309.8) * mm, "end": v(-6.18, -309.8) * mm});
            skLineSegment(sketch, "E395", {"start": v(-6.18, -305.04) * mm, "end": v(-6.18, -309.8) * mm});
            skLineSegment(sketch, "E396", {"start": v(-6.18, -305.04) * mm, "end": v(6.18, -305.04) * mm});
            skLineSegment(sketch, "E397", {"start": v(6.18, -305.04) * mm, "end": v(6.18, -309.8) * mm});
            skLineSegment(sketch, "E398", {"start": v(6.18, -309.8) * mm, "end": v(18.53, -309.8) * mm});
            skLineSegment(sketch, "E399", {"start": v(18.53, -305.04) * mm, "end": v(18.53, -309.8) * mm});
            skLineSegment(sketch, "E400", {"start": v(18.53, -305.04) * mm, "end": v(30.9, -305.04) * mm});
            skLineSegment(sketch, "E401", {"start": v(30.9, -305.04) * mm, "end": v(30.9, -309.8) * mm});
            skLineSegment(sketch, "E402", {"start": v(30.9, -309.8) * mm, "end": v(43.25, -309.8) * mm});
            skLineSegment(sketch, "E403", {"start": v(43.25, -305.04) * mm, "end": v(43.25, -309.8) * mm});
            skLineSegment(sketch, "E404", {"start": v(43.25, -305.04) * mm, "end": v(55.6, -305.04) * mm});
            skLineSegment(sketch, "E405", {"start": v(55.6, -305.04) * mm, "end": v(55.6, -309.8) * mm});
            skLineSegment(sketch, "E406", {"start": v(55.6, -309.8) * mm, "end": v(67.96, -309.8) * mm});
            skLineSegment(sketch, "E407", {"start": v(67.96, -305.04) * mm, "end": v(67.96, -309.8) * mm});
            skLineSegment(sketch, "E408", {"start": v(67.96, -305.04) * mm, "end": v(80.32, -305.04) * mm});
            skLineSegment(sketch, "E409", {"start": v(80.32, -305.04) * mm, "end": v(80.32, -309.8) * mm});
            skLineSegment(sketch, "E410", {"start": v(80.32, -309.8) * mm, "end": v(92.67, -309.8) * mm});
            skLineSegment(sketch, "E411", {"start": v(92.67, -305.04) * mm, "end": v(92.67, -309.8) * mm});
            skLineSegment(sketch, "E412", {"start": v(92.67, -305.04) * mm, "end": v(105.03, -305.04) * mm});
            skLineSegment(sketch, "E413", {"start": v(105.03, -305.04) * mm, "end": v(105.03, -309.8) * mm});
            skLineSegment(sketch, "E414", {"start": v(105.03, -309.8) * mm, "end": v(117.39, -309.8) * mm});
            skLineSegment(sketch, "E415", {"start": v(117.39, -305.04) * mm, "end": v(117.39, -309.8) * mm});
            skLineSegment(sketch, "E416", {"start": v(117.39, -305.04) * mm, "end": v(129.75, -305.04) * mm});
            skLineSegment(sketch, "E417", {"start": v(129.75, -305.04) * mm, "end": v(129.75, -309.8) * mm});
            skLineSegment(sketch, "E418", {"start": v(129.75, -309.8) * mm, "end": v(142.1, -309.8) * mm});
            skLineSegment(sketch, "E419", {"start": v(142.1, -305.04) * mm, "end": v(142.1, -309.8) * mm});
            skLineSegment(sketch, "E420", {"start": v(142.1, -305.04) * mm, "end": v(154.46, -305.04) * mm});
            skLineSegment(sketch, "E421", {"start": v(154.46, -305.04) * mm, "end": v(154.46, -309.8) * mm});
            skLineSegment(sketch, "E422", {"start": v(154.46, -309.8) * mm, "end": v(166.82, -309.8) * mm});
            skLineSegment(sketch, "E423", {"start": v(166.82, -305.04) * mm, "end": v(166.82, -309.8) * mm});
            skLineSegment(sketch, "E424", {"start": v(166.82, -305.04) * mm, "end": v(179.17, -305.04) * mm});
            skLineSegment(sketch, "E425", {"start": v(179.17, -305.04) * mm, "end": v(179.17, -309.8) * mm});
            skLineSegment(sketch, "E426", {"start": v(179.17, -309.8) * mm, "end": v(191.53, -309.8) * mm});
            skLineSegment(sketch, "E427", {"start": v(191.53, -305.04) * mm, "end": v(191.53, -309.8) * mm});
            skLineSegment(sketch, "E428", {"start": v(191.53, -305.04) * mm, "end": v(203.89, -305.04) * mm});
            skLineSegment(sketch, "E429", {"start": v(203.89, -305.04) * mm, "end": v(203.89, -309.8) * mm});
            skLineSegment(sketch, "E430", {"start": v(203.89, -309.8) * mm, "end": v(216.25, -309.8) * mm});
            skLineSegment(sketch, "E431", {"start": v(216.25, -305.04) * mm, "end": v(216.25, -309.8) * mm});
            skLineSegment(sketch, "E432", {"start": v(216.25, -305.04) * mm, "end": v(223.84, -305.04) * mm});
            skLineSegment(sketch, "E433", {"start": v(-223.84, -9.76) * mm, "end": v(-216.24, -9.76) * mm});
            skLineSegment(sketch, "E434", {"start": v(-216.24, -5) * mm, "end": v(-216.24, -9.76) * mm});
            skLineSegment(sketch, "E435", {"start": v(-216.24, -5) * mm, "end": v(-203.89, -5) * mm});
            skLineSegment(sketch, "E436", {"start": v(-203.89, -5) * mm, "end": v(-203.89, -9.76) * mm});
            skLineSegment(sketch, "E437", {"start": v(-203.89, -9.76) * mm, "end": v(-191.53, -9.76) * mm});
            skLineSegment(sketch, "E438", {"start": v(-191.53, -5) * mm, "end": v(-191.53, -9.76) * mm});
            skLineSegment(sketch, "E439", {"start": v(-191.53, -5) * mm, "end": v(-179.17, -5) * mm});
            skLineSegment(sketch, "E440", {"start": v(-179.17, -5) * mm, "end": v(-179.17, -9.76) * mm});
            skLineSegment(sketch, "E441", {"start": v(-179.17, -9.76) * mm, "end": v(-166.81, -9.76) * mm});
            skLineSegment(sketch, "E442", {"start": v(-166.81, -5) * mm, "end": v(-166.81, -9.76) * mm});
            skLineSegment(sketch, "E443", {"start": v(-166.81, -5) * mm, "end": v(-154.46, -5) * mm});
            skLineSegment(sketch, "E444", {"start": v(-154.46, -5) * mm, "end": v(-154.46, -9.76) * mm});
            skLineSegment(sketch, "E445", {"start": v(-154.46, -9.76) * mm, "end": v(-142.1, -9.76) * mm});
            skLineSegment(sketch, "E446", {"start": v(-142.1, -5) * mm, "end": v(-142.1, -9.76) * mm});
            skLineSegment(sketch, "E447", {"start": v(-142.1, -5) * mm, "end": v(-129.75, -5) * mm});
            skLineSegment(sketch, "E448", {"start": v(-129.75, -5) * mm, "end": v(-129.75, -9.76) * mm});
            skLineSegment(sketch, "E449", {"start": v(-129.75, -9.76) * mm, "end": v(-117.39, -9.76) * mm});
            skLineSegment(sketch, "E450", {"start": v(-117.39, -5) * mm, "end": v(-117.39, -9.76) * mm});
            skLineSegment(sketch, "E451", {"start": v(-117.39, -5) * mm, "end": v(-105.03, -5) * mm});
            skLineSegment(sketch, "E452", {"start": v(-105.03, -5) * mm, "end": v(-105.03, -9.76) * mm});
            skLineSegment(sketch, "E453", {"start": v(-105.03, -9.76) * mm, "end": v(-92.68, -9.76) * mm});
            skLineSegment(sketch, "E454", {"start": v(-92.68, -5) * mm, "end": v(-92.68, -9.76) * mm});
            skLineSegment(sketch, "E455", {"start": v(-92.68, -5) * mm, "end": v(-80.32, -5) * mm});
            skLineSegment(sketch, "E456", {"start": v(-80.32, -5) * mm, "end": v(-80.32, -9.76) * mm});
            skLineSegment(sketch, "E457", {"start": v(-80.32, -9.76) * mm, "end": v(-67.96, -9.76) * mm});
            skLineSegment(sketch, "E458", {"start": v(-67.96, -5) * mm, "end": v(-67.96, -9.76) * mm});
            skLineSegment(sketch, "E459", {"start": v(-67.96, -5) * mm, "end": v(-55.6, -5) * mm});
            skLineSegment(sketch, "E460", {"start": v(-55.6, -5) * mm, "end": v(-55.6, -9.76) * mm});
            skLineSegment(sketch, "E461", {"start": v(-55.6, -9.76) * mm, "end": v(-43.25, -9.76) * mm});
            skLineSegment(sketch, "E462", {"start": v(-43.25, -5) * mm, "end": v(-43.25, -9.76) * mm});
            skLineSegment(sketch, "E463", {"start": v(-43.25, -5) * mm, "end": v(-30.89, -5) * mm});
            skLineSegment(sketch, "E464", {"start": v(-30.89, -5) * mm, "end": v(-30.89, -9.76) * mm});
            skLineSegment(sketch, "E465", {"start": v(-30.89, -9.76) * mm, "end": v(-18.54, -9.76) * mm});
            skLineSegment(sketch, "E466", {"start": v(-18.54, -5) * mm, "end": v(-18.54, -9.76) * mm});
            skLineSegment(sketch, "E467", {"start": v(-18.54, -5) * mm, "end": v(-6.18, -5) * mm});
            skLineSegment(sketch, "E468", {"start": v(-6.18, -5) * mm, "end": v(-6.18, -9.76) * mm});
            skLineSegment(sketch, "E469", {"start": v(-6.18, -9.76) * mm, "end": v(6.18, -9.76) * mm});
            skLineSegment(sketch, "E470", {"start": v(6.18, -5) * mm, "end": v(6.18, -9.76) * mm});
            skLineSegment(sketch, "E471", {"start": v(6.18, -5) * mm, "end": v(18.53, -5) * mm});
            skLineSegment(sketch, "E472", {"start": v(18.53, -5) * mm, "end": v(18.53, -9.76) * mm});
            skLineSegment(sketch, "E473", {"start": v(18.53, -9.76) * mm, "end": v(30.9, -9.76) * mm});
            skLineSegment(sketch, "E474", {"start": v(30.9, -5) * mm, "end": v(30.9, -9.76) * mm});
            skLineSegment(sketch, "E475", {"start": v(30.9, -5) * mm, "end": v(43.25, -5) * mm});
            skLineSegment(sketch, "E476", {"start": v(43.25, -5) * mm, "end": v(43.25, -9.76) * mm});
            skLineSegment(sketch, "E477", {"start": v(43.25, -9.76) * mm, "end": v(55.6, -9.76) * mm});
            skLineSegment(sketch, "E478", {"start": v(55.6, -5) * mm, "end": v(55.6, -9.76) * mm});
            skLineSegment(sketch, "E479", {"start": v(55.6, -5) * mm, "end": v(67.96, -5) * mm});
            skLineSegment(sketch, "E480", {"start": v(67.96, -5) * mm, "end": v(67.96, -9.76) * mm});
            skLineSegment(sketch, "E481", {"start": v(67.96, -9.76) * mm, "end": v(80.32, -9.76) * mm});
            skLineSegment(sketch, "E482", {"start": v(80.32, -5) * mm, "end": v(80.32, -9.76) * mm});
            skLineSegment(sketch, "E483", {"start": v(80.32, -5) * mm, "end": v(92.67, -5) * mm});
            skLineSegment(sketch, "E484", {"start": v(92.67, -5) * mm, "end": v(92.67, -9.76) * mm});
            skLineSegment(sketch, "E485", {"start": v(92.67, -9.76) * mm, "end": v(105.03, -9.76) * mm});
            skLineSegment(sketch, "E486", {"start": v(105.03, -5) * mm, "end": v(105.03, -9.76) * mm});
            skLineSegment(sketch, "E487", {"start": v(105.03, -5) * mm, "end": v(117.39, -5) * mm});
            skLineSegment(sketch, "E488", {"start": v(117.39, -5) * mm, "end": v(117.39, -9.76) * mm});
            skLineSegment(sketch, "E489", {"start": v(117.39, -9.76) * mm, "end": v(129.75, -9.76) * mm});
            skLineSegment(sketch, "E490", {"start": v(129.75, -5) * mm, "end": v(129.75, -9.76) * mm});
            skLineSegment(sketch, "E491", {"start": v(129.75, -5) * mm, "end": v(142.1, -5) * mm});
            skLineSegment(sketch, "E492", {"start": v(142.1, -5) * mm, "end": v(142.1, -9.76) * mm});
            skLineSegment(sketch, "E493", {"start": v(142.1, -9.76) * mm, "end": v(154.46, -9.76) * mm});
            skLineSegment(sketch, "E494", {"start": v(154.46, -5) * mm, "end": v(154.46, -9.76) * mm});
            skLineSegment(sketch, "E495", {"start": v(154.46, -5) * mm, "end": v(166.82, -5) * mm});
            skLineSegment(sketch, "E496", {"start": v(166.82, -5) * mm, "end": v(166.82, -9.76) * mm});
            skLineSegment(sketch, "E497", {"start": v(166.82, -9.76) * mm, "end": v(179.17, -9.76) * mm});
            skLineSegment(sketch, "E498", {"start": v(179.17, -5) * mm, "end": v(179.17, -9.76) * mm});
            skLineSegment(sketch, "E499", {"start": v(179.17, -5) * mm, "end": v(191.53, -5) * mm});
            skLineSegment(sketch, "E500", {"start": v(191.53, -5) * mm, "end": v(191.53, -9.76) * mm});
            skLineSegment(sketch, "E501", {"start": v(191.53, -9.76) * mm, "end": v(203.89, -9.76) * mm});
            skLineSegment(sketch, "E502", {"start": v(203.89, -5) * mm, "end": v(203.89, -9.76) * mm});
            skLineSegment(sketch, "E503", {"start": v(203.89, -5) * mm, "end": v(216.25, -5) * mm});
            skLineSegment(sketch, "E504", {"start": v(216.25, -5) * mm, "end": v(216.25, -9.76) * mm});
            skLineSegment(sketch, "E505", {"start": v(216.25, -9.76) * mm, "end": v(223.84, -9.76) * mm});
            skLineSegment(sketch, "E506", {"start": v(-223.84, -305.04) * mm, "end": v(-223.84, -297.6) * mm});
            skLineSegment(sketch, "E507", {"start": v(-223.84, -297.6) * mm, "end": v(-228.6, -297.6) * mm});
            skLineSegment(sketch, "E508", {"start": v(-228.6, -297.6) * mm, "end": v(-228.6, -285.42) * mm});
            skLineSegment(sketch, "E509", {"start": v(-223.84, -285.42) * mm, "end": v(-228.6, -285.42) * mm});
            skLineSegment(sketch, "E510", {"start": v(-223.84, -285.42) * mm, "end": v(-223.84, -273.23) * mm});
            skLineSegment(sketch, "E511", {"start": v(-223.84, -273.23) * mm, "end": v(-228.6, -273.23) * mm});
            skLineSegment(sketch, "E512", {"start": v(-228.6, -273.23) * mm, "end": v(-228.6, -261.03) * mm});
            skLineSegment(sketch, "E513", {"start": v(-223.84, -261.03) * mm, "end": v(-228.6, -261.03) * mm});
            skLineSegment(sketch, "E514", {"start": v(-223.84, -261.03) * mm, "end": v(-223.84, -248.84) * mm});
            skLineSegment(sketch, "E515", {"start": v(-223.84, -248.84) * mm, "end": v(-228.6, -248.84) * mm});
            skLineSegment(sketch, "E516", {"start": v(-228.6, -248.84) * mm, "end": v(-228.6, -236.65) * mm});
            skLineSegment(sketch, "E517", {"start": v(-223.84, -236.65) * mm, "end": v(-228.6, -236.65) * mm});
            skLineSegment(sketch, "E518", {"start": v(-223.84, -236.65) * mm, "end": v(-223.84, -224.46) * mm});
            skLineSegment(sketch, "E519", {"start": v(-223.84, -224.46) * mm, "end": v(-228.6, -224.46) * mm});
            skLineSegment(sketch, "E520", {"start": v(-228.6, -224.46) * mm, "end": v(-228.6, -212.27) * mm});
            skLineSegment(sketch, "E521", {"start": v(-223.84, -212.27) * mm, "end": v(-228.6, -212.27) * mm});
            skLineSegment(sketch, "E522", {"start": v(-223.84, -212.27) * mm, "end": v(-223.84, -200.07) * mm});
            skLineSegment(sketch, "E523", {"start": v(-223.84, -200.07) * mm, "end": v(-228.6, -200.07) * mm});
            skLineSegment(sketch, "E524", {"start": v(-228.6, -200.07) * mm, "end": v(-228.6, -187.88) * mm});
            skLineSegment(sketch, "E525", {"start": v(-223.84, -187.88) * mm, "end": v(-228.6, -187.88) * mm});
            skLineSegment(sketch, "E526", {"start": v(-223.84, -187.88) * mm, "end": v(-223.84, -175.69) * mm});
            skLineSegment(sketch, "E527", {"start": v(-223.84, -175.69) * mm, "end": v(-228.6, -175.69) * mm});
            skLineSegment(sketch, "E528", {"start": v(-228.6, -175.69) * mm, "end": v(-228.6, -163.5) * mm});
            skLineSegment(sketch, "E529", {"start": v(-223.84, -163.5) * mm, "end": v(-228.6, -163.5) * mm});
            skLineSegment(sketch, "E530", {"start": v(-223.84, -163.5) * mm, "end": v(-223.84, -151.3) * mm});
            skLineSegment(sketch, "E531", {"start": v(-223.84, -151.3) * mm, "end": v(-228.6, -151.3) * mm});
            skLineSegment(sketch, "E532", {"start": v(-228.6, -151.3) * mm, "end": v(-228.6, -139.11) * mm});
            skLineSegment(sketch, "E533", {"start": v(-223.84, -139.11) * mm, "end": v(-228.6, -139.11) * mm});
            skLineSegment(sketch, "E534", {"start": v(-223.84, -139.11) * mm, "end": v(-223.84, -126.92) * mm});
            skLineSegment(sketch, "E535", {"start": v(-223.84, -126.92) * mm, "end": v(-228.6, -126.92) * mm});
            skLineSegment(sketch, "E536", {"start": v(-228.6, -126.92) * mm, "end": v(-228.6, -114.73) * mm});
            skLineSegment(sketch, "E537", {"start": v(-223.84, -114.73) * mm, "end": v(-228.6, -114.73) * mm});
            skLineSegment(sketch, "E538", {"start": v(-223.84, -114.73) * mm, "end": v(-223.84, -102.54) * mm});
            skLineSegment(sketch, "E539", {"start": v(-223.84, -102.54) * mm, "end": v(-228.6, -102.54) * mm});
            skLineSegment(sketch, "E540", {"start": v(-228.6, -102.54) * mm, "end": v(-228.6, -90.35) * mm});
            skLineSegment(sketch, "E541", {"start": v(-223.84, -90.35) * mm, "end": v(-228.6, -90.35) * mm});
            skLineSegment(sketch, "E542", {"start": v(-223.84, -90.35) * mm, "end": v(-223.84, -78.15) * mm});
            skLineSegment(sketch, "E543", {"start": v(-223.84, -78.15) * mm, "end": v(-228.6, -78.15) * mm});
            skLineSegment(sketch, "E544", {"start": v(-228.6, -78.15) * mm, "end": v(-228.6, -65.96) * mm});
            skLineSegment(sketch, "E545", {"start": v(-223.84, -65.96) * mm, "end": v(-228.6, -65.96) * mm});
            skLineSegment(sketch, "E546", {"start": v(-223.84, -65.96) * mm, "end": v(-223.84, -53.77) * mm});
            skLineSegment(sketch, "E547", {"start": v(-223.84, -53.77) * mm, "end": v(-228.6, -53.77) * mm});
            skLineSegment(sketch, "E548", {"start": v(-228.6, -53.77) * mm, "end": v(-228.6, -41.58) * mm});
            skLineSegment(sketch, "E549", {"start": v(-223.84, -41.58) * mm, "end": v(-228.6, -41.58) * mm});
            skLineSegment(sketch, "E550", {"start": v(-223.84, -41.58) * mm, "end": v(-223.84, -29.39) * mm});
            skLineSegment(sketch, "E551", {"start": v(-223.84, -29.39) * mm, "end": v(-228.6, -29.39) * mm});
            skLineSegment(sketch, "E552", {"start": v(-228.6, -29.39) * mm, "end": v(-228.6, -17.2) * mm});
            skLineSegment(sketch, "E553", {"start": v(-223.84, -17.2) * mm, "end": v(-228.6, -17.2) * mm});
            skLineSegment(sketch, "E554", {"start": v(-223.84, -17.2) * mm, "end": v(-223.84, -9.76) * mm});
            skLineSegment(sketch, "E555", {"start": v(223.84, -305.04) * mm, "end": v(223.84, -297.6) * mm});
            skLineSegment(sketch, "E556", {"start": v(228.6, -297.6) * mm, "end": v(223.84, -297.6) * mm});
            skLineSegment(sketch, "E557", {"start": v(228.6, -297.6) * mm, "end": v(228.6, -285.42) * mm});
            skLineSegment(sketch, "E558", {"start": v(228.6, -285.42) * mm, "end": v(223.84, -285.42) * mm});
            skLineSegment(sketch, "E559", {"start": v(223.84, -285.42) * mm, "end": v(223.84, -273.23) * mm});
            skLineSegment(sketch, "E560", {"start": v(228.6, -273.23) * mm, "end": v(223.84, -273.23) * mm});
            skLineSegment(sketch, "E561", {"start": v(228.6, -273.23) * mm, "end": v(228.6, -261.03) * mm});
            skLineSegment(sketch, "E562", {"start": v(228.6, -261.03) * mm, "end": v(223.84, -261.03) * mm});
            skLineSegment(sketch, "E563", {"start": v(223.84, -261.03) * mm, "end": v(223.84, -248.84) * mm});
            skLineSegment(sketch, "E564", {"start": v(228.6, -248.84) * mm, "end": v(223.84, -248.84) * mm});
            skLineSegment(sketch, "E565", {"start": v(228.6, -248.84) * mm, "end": v(228.6, -236.65) * mm});
            skLineSegment(sketch, "E566", {"start": v(228.6, -236.65) * mm, "end": v(223.84, -236.65) * mm});
            skLineSegment(sketch, "E567", {"start": v(223.84, -236.65) * mm, "end": v(223.84, -224.46) * mm});
            skLineSegment(sketch, "E568", {"start": v(228.6, -224.46) * mm, "end": v(223.84, -224.46) * mm});
            skLineSegment(sketch, "E569", {"start": v(228.6, -224.46) * mm, "end": v(228.6, -212.27) * mm});
            skLineSegment(sketch, "E570", {"start": v(228.6, -212.27) * mm, "end": v(223.84, -212.27) * mm});
            skLineSegment(sketch, "E571", {"start": v(223.84, -212.27) * mm, "end": v(223.84, -200.07) * mm});
            skLineSegment(sketch, "E572", {"start": v(228.6, -200.07) * mm, "end": v(223.84, -200.07) * mm});
            skLineSegment(sketch, "E573", {"start": v(228.6, -200.07) * mm, "end": v(228.6, -187.88) * mm});
            skLineSegment(sketch, "E574", {"start": v(228.6, -187.88) * mm, "end": v(223.84, -187.88) * mm});
            skLineSegment(sketch, "E575", {"start": v(223.84, -187.88) * mm, "end": v(223.84, -175.69) * mm});
            skLineSegment(sketch, "E576", {"start": v(228.6, -175.69) * mm, "end": v(223.84, -175.69) * mm});
            skLineSegment(sketch, "E577", {"start": v(228.6, -175.69) * mm, "end": v(228.6, -163.5) * mm});
            skLineSegment(sketch, "E578", {"start": v(228.6, -163.5) * mm, "end": v(223.84, -163.5) * mm});
            skLineSegment(sketch, "E579", {"start": v(223.84, -163.5) * mm, "end": v(223.84, -151.3) * mm});
            skLineSegment(sketch, "E580", {"start": v(228.6, -151.3) * mm, "end": v(223.84, -151.3) * mm});
            skLineSegment(sketch, "E581", {"start": v(228.6, -151.3) * mm, "end": v(228.6, -139.11) * mm});
            skLineSegment(sketch, "E582", {"start": v(228.6, -139.11) * mm, "end": v(223.84, -139.11) * mm});
            skLineSegment(sketch, "E583", {"start": v(223.84, -139.11) * mm, "end": v(223.84, -126.92) * mm});
            skLineSegment(sketch, "E584", {"start": v(228.6, -126.92) * mm, "end": v(223.84, -126.92) * mm});
            skLineSegment(sketch, "E585", {"start": v(228.6, -126.92) * mm, "end": v(228.6, -114.73) * mm});
            skLineSegment(sketch, "E586", {"start": v(228.6, -114.73) * mm, "end": v(223.84, -114.73) * mm});
            skLineSegment(sketch, "E587", {"start": v(223.84, -114.73) * mm, "end": v(223.84, -102.54) * mm});
            skLineSegment(sketch, "E588", {"start": v(228.6, -102.54) * mm, "end": v(223.84, -102.54) * mm});
            skLineSegment(sketch, "E589", {"start": v(228.6, -102.54) * mm, "end": v(228.6, -90.35) * mm});
            skLineSegment(sketch, "E590", {"start": v(228.6, -90.35) * mm, "end": v(223.84, -90.35) * mm});
            skLineSegment(sketch, "E591", {"start": v(223.84, -90.35) * mm, "end": v(223.84, -78.15) * mm});
            skLineSegment(sketch, "E592", {"start": v(228.6, -78.15) * mm, "end": v(223.84, -78.15) * mm});
            skLineSegment(sketch, "E593", {"start": v(228.6, -78.15) * mm, "end": v(228.6, -65.96) * mm});
            skLineSegment(sketch, "E594", {"start": v(228.6, -65.96) * mm, "end": v(223.84, -65.96) * mm});
            skLineSegment(sketch, "E595", {"start": v(223.84, -65.96) * mm, "end": v(223.84, -53.77) * mm});
            skLineSegment(sketch, "E596", {"start": v(228.6, -53.77) * mm, "end": v(223.84, -53.77) * mm});
            skLineSegment(sketch, "E597", {"start": v(228.6, -53.77) * mm, "end": v(228.6, -41.58) * mm});
            skLineSegment(sketch, "E598", {"start": v(228.6, -41.58) * mm, "end": v(223.84, -41.58) * mm});
            skLineSegment(sketch, "E599", {"start": v(223.84, -41.58) * mm, "end": v(223.84, -29.39) * mm});
            skLineSegment(sketch, "E600", {"start": v(228.6, -29.39) * mm, "end": v(223.84, -29.39) * mm});
            skLineSegment(sketch, "E601", {"start": v(228.6, -29.39) * mm, "end": v(228.6, -17.2) * mm});
            skLineSegment(sketch, "E602", {"start": v(228.6, -17.2) * mm, "end": v(223.84, -17.2) * mm});
            skLineSegment(sketch, "E603", {"start": v(223.84, -17.2) * mm, "end": v(223.84, -9.76) * mm});
            skLineSegment(sketch, "E604", {"start": v(238.6, -309.8) * mm, "end": v(250.8, -309.8) * mm});
            skLineSegment(sketch, "E605", {"start": v(250.8, -305.04) * mm, "end": v(250.8, -309.8) * mm});
            skLineSegment(sketch, "E606", {"start": v(250.8, -305.04) * mm, "end": v(262.98, -305.04) * mm});
            skLineSegment(sketch, "E607", {"start": v(262.98, -305.04) * mm, "end": v(262.98, -309.8) * mm});
            skLineSegment(sketch, "E608", {"start": v(262.98, -309.8) * mm, "end": v(275.18, -309.8) * mm});
            skLineSegment(sketch, "E609", {"start": v(275.18, -305.04) * mm, "end": v(275.18, -309.8) * mm});
            skLineSegment(sketch, "E610", {"start": v(275.18, -305.04) * mm, "end": v(287.37, -305.04) * mm});
            skLineSegment(sketch, "E611", {"start": v(287.37, -305.04) * mm, "end": v(287.37, -309.8) * mm});
            skLineSegment(sketch, "E612", {"start": v(287.37, -309.8) * mm, "end": v(299.56, -309.8) * mm});
            skLineSegment(sketch, "E613", {"start": v(299.56, -305.04) * mm, "end": v(299.56, -309.8) * mm});
            skLineSegment(sketch, "E614", {"start": v(299.56, -305.04) * mm, "end": v(311.75, -305.04) * mm});
            skLineSegment(sketch, "E615", {"start": v(311.75, -305.04) * mm, "end": v(311.75, -309.8) * mm});
            skLineSegment(sketch, "E616", {"start": v(311.75, -309.8) * mm, "end": v(323.94, -309.8) * mm});
            skLineSegment(sketch, "E617", {"start": v(323.94, -305.04) * mm, "end": v(323.94, -309.8) * mm});
            skLineSegment(sketch, "E618", {"start": v(323.94, -305.04) * mm, "end": v(336.14, -305.04) * mm});
            skLineSegment(sketch, "E619", {"start": v(336.14, -305.04) * mm, "end": v(336.14, -309.8) * mm});
            skLineSegment(sketch, "E620", {"start": v(336.14, -309.8) * mm, "end": v(348.33, -309.8) * mm});
            skLineSegment(sketch, "E621", {"start": v(348.33, -305.04) * mm, "end": v(348.33, -309.8) * mm});
            skLineSegment(sketch, "E622", {"start": v(348.33, -305.04) * mm, "end": v(360.52, -305.04) * mm});
            skLineSegment(sketch, "E623", {"start": v(360.52, -305.04) * mm, "end": v(360.52, -309.8) * mm});
            skLineSegment(sketch, "E624", {"start": v(360.52, -309.8) * mm, "end": v(372.71, -309.8) * mm});
            skLineSegment(sketch, "E625", {"start": v(372.71, -305.04) * mm, "end": v(372.71, -309.8) * mm});
            skLineSegment(sketch, "E626", {"start": v(372.71, -305.04) * mm, "end": v(384.9, -305.04) * mm});
            skLineSegment(sketch, "E627", {"start": v(384.9, -305.04) * mm, "end": v(384.9, -309.8) * mm});
            skLineSegment(sketch, "E628", {"start": v(384.9, -309.8) * mm, "end": v(397.1, -309.8) * mm});
            skLineSegment(sketch, "E629", {"start": v(397.1, -305.04) * mm, "end": v(397.1, -309.8) * mm});
            skLineSegment(sketch, "E630", {"start": v(397.1, -305.04) * mm, "end": v(409.29, -305.04) * mm});
            skLineSegment(sketch, "E631", {"start": v(409.29, -305.04) * mm, "end": v(409.29, -309.8) * mm});
            skLineSegment(sketch, "E632", {"start": v(409.29, -309.8) * mm, "end": v(421.48, -309.8) * mm});
            skLineSegment(sketch, "E633", {"start": v(421.48, -305.04) * mm, "end": v(421.48, -309.8) * mm});
            skLineSegment(sketch, "E634", {"start": v(421.48, -305.04) * mm, "end": v(433.67, -305.04) * mm});
            skLineSegment(sketch, "E635", {"start": v(433.67, -305.04) * mm, "end": v(433.67, -309.8) * mm});
            skLineSegment(sketch, "E636", {"start": v(433.67, -309.8) * mm, "end": v(445.86, -309.8) * mm});
            skLineSegment(sketch, "E637", {"start": v(445.86, -305.04) * mm, "end": v(445.86, -309.8) * mm});
            skLineSegment(sketch, "E638", {"start": v(445.86, -305.04) * mm, "end": v(458.06, -305.04) * mm});
            skLineSegment(sketch, "E639", {"start": v(458.06, -305.04) * mm, "end": v(458.06, -309.8) * mm});
            skLineSegment(sketch, "E640", {"start": v(458.06, -309.8) * mm, "end": v(470.25, -309.8) * mm});
            skLineSegment(sketch, "E641", {"start": v(470.25, -305.04) * mm, "end": v(470.25, -309.8) * mm});
            skLineSegment(sketch, "E642", {"start": v(470.25, -305.04) * mm, "end": v(482.44, -305.04) * mm});
            skLineSegment(sketch, "E643", {"start": v(482.44, -305.04) * mm, "end": v(482.44, -309.8) * mm});
            skLineSegment(sketch, "E644", {"start": v(482.44, -309.8) * mm, "end": v(494.63, -309.8) * mm});
            skLineSegment(sketch, "E645", {"start": v(494.63, -305.04) * mm, "end": v(494.63, -309.8) * mm});
            skLineSegment(sketch, "E646", {"start": v(494.63, -305.04) * mm, "end": v(506.82, -305.04) * mm});
            skLineSegment(sketch, "E647", {"start": v(506.82, -305.04) * mm, "end": v(506.82, -309.8) * mm});
            skLineSegment(sketch, "E648", {"start": v(506.82, -309.8) * mm, "end": v(519.02, -309.8) * mm});
            skLineSegment(sketch, "E649", {"start": v(519.02, -305.04) * mm, "end": v(519.02, -309.8) * mm});
            skLineSegment(sketch, "E650", {"start": v(519.02, -305.04) * mm, "end": v(531.2, -305.04) * mm});
            skLineSegment(sketch, "E651", {"start": v(531.2, -305.04) * mm, "end": v(531.2, -309.8) * mm});
            skLineSegment(sketch, "E652", {"start": v(531.2, -309.8) * mm, "end": v(538.64, -309.8) * mm});
            skLineSegment(sketch, "E653", {"start": v(238.6, -132) * mm, "end": v(250.8, -132) * mm});
            skLineSegment(sketch, "E654", {"start": v(250.8, -132) * mm, "end": v(250.8, -136.76) * mm});
            skLineSegment(sketch, "E655", {"start": v(250.8, -136.76) * mm, "end": v(262.98, -136.76) * mm});
            skLineSegment(sketch, "E656", {"start": v(262.98, -132) * mm, "end": v(262.98, -136.76) * mm});
            skLineSegment(sketch, "E657", {"start": v(262.98, -132) * mm, "end": v(275.18, -132) * mm});
            skLineSegment(sketch, "E658", {"start": v(275.18, -132) * mm, "end": v(275.18, -136.76) * mm});
            skLineSegment(sketch, "E659", {"start": v(275.18, -136.76) * mm, "end": v(287.37, -136.76) * mm});
            skLineSegment(sketch, "E660", {"start": v(287.37, -132) * mm, "end": v(287.37, -136.76) * mm});
            skLineSegment(sketch, "E661", {"start": v(287.37, -132) * mm, "end": v(299.56, -132) * mm});
            skLineSegment(sketch, "E662", {"start": v(299.56, -132) * mm, "end": v(299.56, -136.76) * mm});
            skLineSegment(sketch, "E663", {"start": v(299.56, -136.76) * mm, "end": v(311.75, -136.76) * mm});
            skLineSegment(sketch, "E664", {"start": v(311.75, -132) * mm, "end": v(311.75, -136.76) * mm});
            skLineSegment(sketch, "E665", {"start": v(311.75, -132) * mm, "end": v(323.94, -132) * mm});
            skLineSegment(sketch, "E666", {"start": v(323.94, -132) * mm, "end": v(323.94, -136.76) * mm});
            skLineSegment(sketch, "E667", {"start": v(323.94, -136.76) * mm, "end": v(336.14, -136.76) * mm});
            skLineSegment(sketch, "E668", {"start": v(336.14, -132) * mm, "end": v(336.14, -136.76) * mm});
            skLineSegment(sketch, "E669", {"start": v(336.14, -132) * mm, "end": v(348.33, -132) * mm});
            skLineSegment(sketch, "E670", {"start": v(348.33, -132) * mm, "end": v(348.33, -136.76) * mm});
            skLineSegment(sketch, "E671", {"start": v(348.33, -136.76) * mm, "end": v(360.52, -136.76) * mm});
            skLineSegment(sketch, "E672", {"start": v(360.52, -132) * mm, "end": v(360.52, -136.76) * mm});
            skLineSegment(sketch, "E673", {"start": v(360.52, -132) * mm, "end": v(372.71, -132) * mm});
            skLineSegment(sketch, "E674", {"start": v(372.71, -132) * mm, "end": v(372.71, -136.76) * mm});
            skLineSegment(sketch, "E675", {"start": v(372.71, -136.76) * mm, "end": v(384.9, -136.76) * mm});
            skLineSegment(sketch, "E676", {"start": v(384.9, -132) * mm, "end": v(384.9, -136.76) * mm});
            skLineSegment(sketch, "E677", {"start": v(384.9, -132) * mm, "end": v(397.1, -132) * mm});
            skLineSegment(sketch, "E678", {"start": v(397.1, -132) * mm, "end": v(397.1, -136.76) * mm});
            skLineSegment(sketch, "E679", {"start": v(397.1, -136.76) * mm, "end": v(409.29, -136.76) * mm});
            skLineSegment(sketch, "E680", {"start": v(409.29, -132) * mm, "end": v(409.29, -136.76) * mm});
            skLineSegment(sketch, "E681", {"start": v(409.29, -132) * mm, "end": v(421.48, -132) * mm});
            skLineSegment(sketch, "E682", {"start": v(421.48, -132) * mm, "end": v(421.48, -136.76) * mm});
            skLineSegment(sketch, "E683", {"start": v(421.48, -136.76) * mm, "end": v(433.67, -136.76) * mm});
            skLineSegment(sketch, "E684", {"start": v(433.67, -132) * mm, "end": v(433.67, -136.76) * mm});
            skLineSegment(sketch, "E685", {"start": v(433.67, -132) * mm, "end": v(445.86, -132) * mm});
            skLineSegment(sketch, "E686", {"start": v(445.86, -132) * mm, "end": v(445.86, -136.76) * mm});
            skLineSegment(sketch, "E687", {"start": v(445.86, -136.76) * mm, "end": v(458.06, -136.76) * mm});
            skLineSegment(sketch, "E688", {"start": v(458.06, -132) * mm, "end": v(458.06, -136.76) * mm});
            skLineSegment(sketch, "E689", {"start": v(458.06, -132) * mm, "end": v(470.25, -132) * mm});
            skLineSegment(sketch, "E690", {"start": v(470.25, -132) * mm, "end": v(470.25, -136.76) * mm});
            skLineSegment(sketch, "E691", {"start": v(470.25, -136.76) * mm, "end": v(482.44, -136.76) * mm});
            skLineSegment(sketch, "E692", {"start": v(482.44, -132) * mm, "end": v(482.44, -136.76) * mm});
            skLineSegment(sketch, "E693", {"start": v(482.44, -132) * mm, "end": v(494.63, -132) * mm});
            skLineSegment(sketch, "E694", {"start": v(494.63, -132) * mm, "end": v(494.63, -136.76) * mm});
            skLineSegment(sketch, "E695", {"start": v(494.63, -136.76) * mm, "end": v(506.82, -136.76) * mm});
            skLineSegment(sketch, "E696", {"start": v(506.82, -132) * mm, "end": v(506.82, -136.76) * mm});
            skLineSegment(sketch, "E697", {"start": v(506.82, -132) * mm, "end": v(519.02, -132) * mm});
            skLineSegment(sketch, "E698", {"start": v(519.02, -132) * mm, "end": v(519.02, -136.76) * mm});
            skLineSegment(sketch, "E699", {"start": v(519.02, -136.76) * mm, "end": v(531.2, -136.76) * mm});
            skLineSegment(sketch, "E700", {"start": v(531.2, -132) * mm, "end": v(531.2, -136.76) * mm});
            skLineSegment(sketch, "E701", {"start": v(531.2, -132) * mm, "end": v(538.64, -132) * mm});
            skLineSegment(sketch, "E702", {"start": v(238.6, -309.8) * mm, "end": v(238.6, -297.95) * mm});
            skLineSegment(sketch, "E703", {"start": v(243.36, -297.95) * mm, "end": v(238.6, -297.95) * mm});
            skLineSegment(sketch, "E704", {"start": v(243.36, -297.95) * mm, "end": v(243.36, -286.1) * mm});
            skLineSegment(sketch, "E705", {"start": v(243.36, -286.1) * mm, "end": v(238.6, -286.1) * mm});
            skLineSegment(sketch, "E706", {"start": v(238.6, -286.1) * mm, "end": v(238.6, -274.24) * mm});
            skLineSegment(sketch, "E707", {"start": v(243.36, -274.24) * mm, "end": v(238.6, -274.24) * mm});
            skLineSegment(sketch, "E708", {"start": v(243.36, -274.24) * mm, "end": v(243.36, -262.39) * mm});
            skLineSegment(sketch, "E709", {"start": v(243.36, -262.39) * mm, "end": v(238.6, -262.39) * mm});
            skLineSegment(sketch, "E710", {"start": v(238.6, -262.39) * mm, "end": v(238.6, -250.54) * mm});
            skLineSegment(sketch, "E711", {"start": v(243.36, -250.54) * mm, "end": v(238.6, -250.54) * mm});
            skLineSegment(sketch, "E712", {"start": v(243.36, -250.54) * mm, "end": v(243.36, -238.68) * mm});
            skLineSegment(sketch, "E713", {"start": v(243.36, -238.68) * mm, "end": v(238.6, -238.68) * mm});
            skLineSegment(sketch, "E714", {"start": v(238.6, -238.68) * mm, "end": v(238.6, -226.83) * mm});
            skLineSegment(sketch, "E715", {"start": v(243.36, -226.83) * mm, "end": v(238.6, -226.83) * mm});
            skLineSegment(sketch, "E716", {"start": v(243.36, -226.83) * mm, "end": v(243.36, -214.98) * mm});
            skLineSegment(sketch, "E717", {"start": v(243.36, -214.98) * mm, "end": v(238.6, -214.98) * mm});
            skLineSegment(sketch, "E718", {"start": v(238.6, -214.98) * mm, "end": v(238.6, -203.12) * mm});
            skLineSegment(sketch, "E719", {"start": v(243.36, -203.12) * mm, "end": v(238.6, -203.12) * mm});
            skLineSegment(sketch, "E720", {"start": v(243.36, -203.12) * mm, "end": v(243.36, -191.27) * mm});
            skLineSegment(sketch, "E721", {"start": v(243.36, -191.27) * mm, "end": v(238.6, -191.27) * mm});
            skLineSegment(sketch, "E722", {"start": v(238.6, -191.27) * mm, "end": v(238.6, -179.42) * mm});
            skLineSegment(sketch, "E723", {"start": v(243.36, -179.42) * mm, "end": v(238.6, -179.42) * mm});
            skLineSegment(sketch, "E724", {"start": v(243.36, -179.42) * mm, "end": v(243.36, -167.56) * mm});
            skLineSegment(sketch, "E725", {"start": v(243.36, -167.56) * mm, "end": v(238.6, -167.56) * mm});
            skLineSegment(sketch, "E726", {"start": v(238.6, -167.56) * mm, "end": v(238.6, -155.7) * mm});
            skLineSegment(sketch, "E727", {"start": v(243.36, -155.7) * mm, "end": v(238.6, -155.7) * mm});
            skLineSegment(sketch, "E728", {"start": v(243.36, -155.7) * mm, "end": v(243.36, -143.86) * mm});
            skLineSegment(sketch, "E729", {"start": v(243.36, -143.86) * mm, "end": v(238.6, -143.86) * mm});
            skLineSegment(sketch, "E730", {"start": v(238.6, -143.86) * mm, "end": v(238.6, -132) * mm});
            skLineSegment(sketch, "E731", {"start": v(538.64, -309.8) * mm, "end": v(538.64, -297.95) * mm});
            skLineSegment(sketch, "E732", {"start": v(543.4, -297.95) * mm, "end": v(538.64, -297.95) * mm});
            skLineSegment(sketch, "E733", {"start": v(543.4, -297.95) * mm, "end": v(543.4, -286.1) * mm});
            skLineSegment(sketch, "E734", {"start": v(543.4, -286.1) * mm, "end": v(538.64, -286.1) * mm});
            skLineSegment(sketch, "E735", {"start": v(538.64, -286.1) * mm, "end": v(538.64, -274.24) * mm});
            skLineSegment(sketch, "E736", {"start": v(543.4, -274.24) * mm, "end": v(538.64, -274.24) * mm});
            skLineSegment(sketch, "E737", {"start": v(543.4, -274.24) * mm, "end": v(543.4, -262.39) * mm});
            skLineSegment(sketch, "E738", {"start": v(543.4, -262.39) * mm, "end": v(538.64, -262.39) * mm});
            skLineSegment(sketch, "E739", {"start": v(538.64, -262.39) * mm, "end": v(538.64, -250.54) * mm});
            skLineSegment(sketch, "E740", {"start": v(543.4, -250.54) * mm, "end": v(538.64, -250.54) * mm});
            skLineSegment(sketch, "E741", {"start": v(543.4, -250.54) * mm, "end": v(543.4, -238.68) * mm});
            skLineSegment(sketch, "E742", {"start": v(543.4, -238.68) * mm, "end": v(538.64, -238.68) * mm});
            skLineSegment(sketch, "E743", {"start": v(538.64, -238.68) * mm, "end": v(538.64, -226.83) * mm});
            skLineSegment(sketch, "E744", {"start": v(543.4, -226.83) * mm, "end": v(538.64, -226.83) * mm});
            skLineSegment(sketch, "E745", {"start": v(543.4, -226.83) * mm, "end": v(543.4, -214.98) * mm});
            skLineSegment(sketch, "E746", {"start": v(543.4, -214.98) * mm, "end": v(538.64, -214.98) * mm});
            skLineSegment(sketch, "E747", {"start": v(538.64, -214.98) * mm, "end": v(538.64, -203.12) * mm});
            skLineSegment(sketch, "E748", {"start": v(543.4, -203.12) * mm, "end": v(538.64, -203.12) * mm});
            skLineSegment(sketch, "E749", {"start": v(543.4, -203.12) * mm, "end": v(543.4, -191.27) * mm});
            skLineSegment(sketch, "E750", {"start": v(543.4, -191.27) * mm, "end": v(538.64, -191.27) * mm});
            skLineSegment(sketch, "E751", {"start": v(538.64, -191.27) * mm, "end": v(538.64, -179.42) * mm});
            skLineSegment(sketch, "E752", {"start": v(543.4, -179.42) * mm, "end": v(538.64, -179.42) * mm});
            skLineSegment(sketch, "E753", {"start": v(543.4, -179.42) * mm, "end": v(543.4, -167.56) * mm});
            skLineSegment(sketch, "E754", {"start": v(543.4, -167.56) * mm, "end": v(538.64, -167.56) * mm});
            skLineSegment(sketch, "E755", {"start": v(538.64, -167.56) * mm, "end": v(538.64, -155.7) * mm});
            skLineSegment(sketch, "E756", {"start": v(543.4, -155.7) * mm, "end": v(538.64, -155.7) * mm});
            skLineSegment(sketch, "E757", {"start": v(543.4, -155.7) * mm, "end": v(543.4, -143.86) * mm});
            skLineSegment(sketch, "E758", {"start": v(543.4, -143.86) * mm, "end": v(538.64, -143.86) * mm});
            skLineSegment(sketch, "E759", {"start": v(538.64, -143.86) * mm, "end": v(538.64, -132) * mm});
            skLineSegment(sketch, "E760", {"start": v(-228.6, 5) * mm, "end": v(-216.24, 5) * mm});
            skLineSegment(sketch, "E761", {"start": v(-216.24, 9.76) * mm, "end": v(-216.24, 5) * mm});
            skLineSegment(sketch, "E762", {"start": v(-216.24, 9.76) * mm, "end": v(-203.89, 9.76) * mm});
            skLineSegment(sketch, "E763", {"start": v(-203.89, 9.76) * mm, "end": v(-203.89, 5) * mm});
            skLineSegment(sketch, "E764", {"start": v(-203.89, 5) * mm, "end": v(-191.53, 5) * mm});
            skLineSegment(sketch, "E765", {"start": v(-191.53, 9.76) * mm, "end": v(-191.53, 5) * mm});
            skLineSegment(sketch, "E766", {"start": v(-191.53, 9.76) * mm, "end": v(-179.17, 9.76) * mm});
            skLineSegment(sketch, "E767", {"start": v(-179.17, 9.76) * mm, "end": v(-179.17, 5) * mm});
            skLineSegment(sketch, "E768", {"start": v(-179.17, 5) * mm, "end": v(-166.81, 5) * mm});
            skLineSegment(sketch, "E769", {"start": v(-166.81, 9.76) * mm, "end": v(-166.81, 5) * mm});
            skLineSegment(sketch, "E770", {"start": v(-166.81, 9.76) * mm, "end": v(-154.46, 9.76) * mm});
            skLineSegment(sketch, "E771", {"start": v(-154.46, 9.76) * mm, "end": v(-154.46, 5) * mm});
            skLineSegment(sketch, "E772", {"start": v(-154.46, 5) * mm, "end": v(-142.1, 5) * mm});
            skLineSegment(sketch, "E773", {"start": v(-142.1, 9.76) * mm, "end": v(-142.1, 5) * mm});
            skLineSegment(sketch, "E774", {"start": v(-142.1, 9.76) * mm, "end": v(-129.75, 9.76) * mm});
            skLineSegment(sketch, "E775", {"start": v(-129.75, 9.76) * mm, "end": v(-129.75, 5) * mm});
            skLineSegment(sketch, "E776", {"start": v(-129.75, 5) * mm, "end": v(-117.39, 5) * mm});
            skLineSegment(sketch, "E777", {"start": v(-117.39, 9.76) * mm, "end": v(-117.39, 5) * mm});
            skLineSegment(sketch, "E778", {"start": v(-117.39, 9.76) * mm, "end": v(-105.03, 9.76) * mm});
            skLineSegment(sketch, "E779", {"start": v(-105.03, 9.76) * mm, "end": v(-105.03, 5) * mm});
            skLineSegment(sketch, "E780", {"start": v(-105.03, 5) * mm, "end": v(-92.68, 5) * mm});
            skLineSegment(sketch, "E781", {"start": v(-92.68, 9.76) * mm, "end": v(-92.68, 5) * mm});
            skLineSegment(sketch, "E782", {"start": v(-92.68, 9.76) * mm, "end": v(-80.32, 9.76) * mm});
            skLineSegment(sketch, "E783", {"start": v(-80.32, 9.76) * mm, "end": v(-80.32, 5) * mm});
            skLineSegment(sketch, "E784", {"start": v(-80.32, 5) * mm, "end": v(-67.96, 5) * mm});
            skLineSegment(sketch, "E785", {"start": v(-67.96, 9.76) * mm, "end": v(-67.96, 5) * mm});
            skLineSegment(sketch, "E786", {"start": v(-67.96, 9.76) * mm, "end": v(-55.6, 9.76) * mm});
            skLineSegment(sketch, "E787", {"start": v(-55.6, 9.76) * mm, "end": v(-55.6, 5) * mm});
            skLineSegment(sketch, "E788", {"start": v(-55.6, 5) * mm, "end": v(-43.25, 5) * mm});
            skLineSegment(sketch, "E789", {"start": v(-43.25, 9.76) * mm, "end": v(-43.25, 5) * mm});
            skLineSegment(sketch, "E790", {"start": v(-43.25, 9.76) * mm, "end": v(-30.89, 9.76) * mm});
            skLineSegment(sketch, "E791", {"start": v(-30.89, 9.76) * mm, "end": v(-30.89, 5) * mm});
            skLineSegment(sketch, "E792", {"start": v(-30.89, 5) * mm, "end": v(-18.54, 5) * mm});
            skLineSegment(sketch, "E793", {"start": v(-18.54, 9.76) * mm, "end": v(-18.54, 5) * mm});
            skLineSegment(sketch, "E794", {"start": v(-18.54, 9.76) * mm, "end": v(-6.18, 9.76) * mm});
            skLineSegment(sketch, "E795", {"start": v(-6.18, 9.76) * mm, "end": v(-6.18, 5) * mm});
            skLineSegment(sketch, "E796", {"start": v(-6.18, 5) * mm, "end": v(6.18, 5) * mm});
            skLineSegment(sketch, "E797", {"start": v(6.18, 9.76) * mm, "end": v(6.18, 5) * mm});
            skLineSegment(sketch, "E798", {"start": v(6.18, 9.76) * mm, "end": v(18.53, 9.76) * mm});
            skLineSegment(sketch, "E799", {"start": v(18.53, 9.76) * mm, "end": v(18.53, 5) * mm});
            skLineSegment(sketch, "E800", {"start": v(18.53, 5) * mm, "end": v(30.9, 5) * mm});
            skLineSegment(sketch, "E801", {"start": v(30.9, 9.76) * mm, "end": v(30.9, 5) * mm});
            skLineSegment(sketch, "E802", {"start": v(30.9, 9.76) * mm, "end": v(43.25, 9.76) * mm});
            skLineSegment(sketch, "E803", {"start": v(43.25, 9.76) * mm, "end": v(43.25, 5) * mm});
            skLineSegment(sketch, "E804", {"start": v(43.25, 5) * mm, "end": v(55.6, 5) * mm});
            skLineSegment(sketch, "E805", {"start": v(55.6, 9.76) * mm, "end": v(55.6, 5) * mm});
            skLineSegment(sketch, "E806", {"start": v(55.6, 9.76) * mm, "end": v(67.96, 9.76) * mm});
            skLineSegment(sketch, "E807", {"start": v(67.96, 9.76) * mm, "end": v(67.96, 5) * mm});
            skLineSegment(sketch, "E808", {"start": v(67.96, 5) * mm, "end": v(80.32, 5) * mm});
            skLineSegment(sketch, "E809", {"start": v(80.32, 9.76) * mm, "end": v(80.32, 5) * mm});
            skLineSegment(sketch, "E810", {"start": v(80.32, 9.76) * mm, "end": v(92.67, 9.76) * mm});
            skLineSegment(sketch, "E811", {"start": v(92.67, 9.76) * mm, "end": v(92.67, 5) * mm});
            skLineSegment(sketch, "E812", {"start": v(92.67, 5) * mm, "end": v(105.03, 5) * mm});
            skLineSegment(sketch, "E813", {"start": v(105.03, 9.76) * mm, "end": v(105.03, 5) * mm});
            skLineSegment(sketch, "E814", {"start": v(105.03, 9.76) * mm, "end": v(117.39, 9.76) * mm});
            skLineSegment(sketch, "E815", {"start": v(117.39, 9.76) * mm, "end": v(117.39, 5) * mm});
            skLineSegment(sketch, "E816", {"start": v(117.39, 5) * mm, "end": v(129.75, 5) * mm});
            skLineSegment(sketch, "E817", {"start": v(129.75, 9.76) * mm, "end": v(129.75, 5) * mm});
            skLineSegment(sketch, "E818", {"start": v(129.75, 9.76) * mm, "end": v(142.1, 9.76) * mm});
            skLineSegment(sketch, "E819", {"start": v(142.1, 9.76) * mm, "end": v(142.1, 5) * mm});
            skLineSegment(sketch, "E820", {"start": v(142.1, 5) * mm, "end": v(154.46, 5) * mm});
            skLineSegment(sketch, "E821", {"start": v(154.46, 9.76) * mm, "end": v(154.46, 5) * mm});
            skLineSegment(sketch, "E822", {"start": v(154.46, 9.76) * mm, "end": v(166.82, 9.76) * mm});
            skLineSegment(sketch, "E823", {"start": v(166.82, 9.76) * mm, "end": v(166.82, 5) * mm});
            skLineSegment(sketch, "E824", {"start": v(166.82, 5) * mm, "end": v(179.17, 5) * mm});
            skLineSegment(sketch, "E825", {"start": v(179.17, 9.76) * mm, "end": v(179.17, 5) * mm});
            skLineSegment(sketch, "E826", {"start": v(179.17, 9.76) * mm, "end": v(191.53, 9.76) * mm});
            skLineSegment(sketch, "E827", {"start": v(191.53, 9.76) * mm, "end": v(191.53, 5) * mm});
            skLineSegment(sketch, "E828", {"start": v(191.53, 5) * mm, "end": v(203.89, 5) * mm});
            skLineSegment(sketch, "E829", {"start": v(203.89, 9.76) * mm, "end": v(203.89, 5) * mm});
            skLineSegment(sketch, "E830", {"start": v(203.89, 9.76) * mm, "end": v(216.25, 9.76) * mm});
            skLineSegment(sketch, "E831", {"start": v(216.25, 9.76) * mm, "end": v(216.25, 5) * mm});
            skLineSegment(sketch, "E832", {"start": v(216.25, 5) * mm, "end": v(223.84, 5) * mm});
            skLineSegment(sketch, "E833", {"start": v(-228.6, 182.8) * mm, "end": v(-216.24, 182.8) * mm});
            skLineSegment(sketch, "E834", {"start": v(-216.24, 182.8) * mm, "end": v(-216.24, 178.04) * mm});
            skLineSegment(sketch, "E835", {"start": v(-216.24, 178.04) * mm, "end": v(-203.89, 178.04) * mm});
            skLineSegment(sketch, "E836", {"start": v(-203.89, 182.8) * mm, "end": v(-203.89, 178.04) * mm});
            skLineSegment(sketch, "E837", {"start": v(-203.89, 182.8) * mm, "end": v(-191.53, 182.8) * mm});
            skLineSegment(sketch, "E838", {"start": v(-191.53, 182.8) * mm, "end": v(-191.53, 178.04) * mm});
            skLineSegment(sketch, "E839", {"start": v(-191.53, 178.04) * mm, "end": v(-179.17, 178.04) * mm});
            skLineSegment(sketch, "E840", {"start": v(-179.17, 182.8) * mm, "end": v(-179.17, 178.04) * mm});
            skLineSegment(sketch, "E841", {"start": v(-179.17, 182.8) * mm, "end": v(-166.81, 182.8) * mm});
            skLineSegment(sketch, "E842", {"start": v(-166.81, 182.8) * mm, "end": v(-166.81, 178.04) * mm});
            skLineSegment(sketch, "E843", {"start": v(-166.81, 178.04) * mm, "end": v(-154.46, 178.04) * mm});
            skLineSegment(sketch, "E844", {"start": v(-154.46, 182.8) * mm, "end": v(-154.46, 178.04) * mm});
            skLineSegment(sketch, "E845", {"start": v(-154.46, 182.8) * mm, "end": v(-142.1, 182.8) * mm});
            skLineSegment(sketch, "E846", {"start": v(-142.1, 182.8) * mm, "end": v(-142.1, 178.04) * mm});
            skLineSegment(sketch, "E847", {"start": v(-142.1, 178.04) * mm, "end": v(-129.75, 178.04) * mm});
            skLineSegment(sketch, "E848", {"start": v(-129.75, 182.8) * mm, "end": v(-129.75, 178.04) * mm});
            skLineSegment(sketch, "E849", {"start": v(-129.75, 182.8) * mm, "end": v(-117.39, 182.8) * mm});
            skLineSegment(sketch, "E850", {"start": v(-117.39, 182.8) * mm, "end": v(-117.39, 178.04) * mm});
            skLineSegment(sketch, "E851", {"start": v(-117.39, 178.04) * mm, "end": v(-105.03, 178.04) * mm});
            skLineSegment(sketch, "E852", {"start": v(-105.03, 182.8) * mm, "end": v(-105.03, 178.04) * mm});
            skLineSegment(sketch, "E853", {"start": v(-105.03, 182.8) * mm, "end": v(-92.68, 182.8) * mm});
            skLineSegment(sketch, "E854", {"start": v(-92.68, 182.8) * mm, "end": v(-92.68, 178.04) * mm});
            skLineSegment(sketch, "E855", {"start": v(-92.68, 178.04) * mm, "end": v(-80.32, 178.04) * mm});
            skLineSegment(sketch, "E856", {"start": v(-80.32, 182.8) * mm, "end": v(-80.32, 178.04) * mm});
            skLineSegment(sketch, "E857", {"start": v(-80.32, 182.8) * mm, "end": v(-67.96, 182.8) * mm});
            skLineSegment(sketch, "E858", {"start": v(-67.96, 182.8) * mm, "end": v(-67.96, 178.04) * mm});
            skLineSegment(sketch, "E859", {"start": v(-67.96, 178.04) * mm, "end": v(-55.6, 178.04) * mm});
            skLineSegment(sketch, "E860", {"start": v(-55.6, 182.8) * mm, "end": v(-55.6, 178.04) * mm});
            skLineSegment(sketch, "E861", {"start": v(-55.6, 182.8) * mm, "end": v(-43.25, 182.8) * mm});
            skLineSegment(sketch, "E862", {"start": v(-43.25, 182.8) * mm, "end": v(-43.25, 178.04) * mm});
            skLineSegment(sketch, "E863", {"start": v(-43.25, 178.04) * mm, "end": v(-30.89, 178.04) * mm});
            skLineSegment(sketch, "E864", {"start": v(-30.89, 182.8) * mm, "end": v(-30.89, 178.04) * mm});
            skLineSegment(sketch, "E865", {"start": v(-30.89, 182.8) * mm, "end": v(-18.54, 182.8) * mm});
            skLineSegment(sketch, "E866", {"start": v(-18.54, 182.8) * mm, "end": v(-18.54, 178.04) * mm});
            skLineSegment(sketch, "E867", {"start": v(-18.54, 178.04) * mm, "end": v(-6.18, 178.04) * mm});
            skLineSegment(sketch, "E868", {"start": v(-6.18, 182.8) * mm, "end": v(-6.18, 178.04) * mm});
            skLineSegment(sketch, "E869", {"start": v(-6.18, 182.8) * mm, "end": v(6.18, 182.8) * mm});
            skLineSegment(sketch, "E870", {"start": v(6.18, 182.8) * mm, "end": v(6.18, 178.04) * mm});
            skLineSegment(sketch, "E871", {"start": v(6.18, 178.04) * mm, "end": v(18.53, 178.04) * mm});
            skLineSegment(sketch, "E872", {"start": v(18.53, 182.8) * mm, "end": v(18.53, 178.04) * mm});
            skLineSegment(sketch, "E873", {"start": v(18.53, 182.8) * mm, "end": v(30.9, 182.8) * mm});
            skLineSegment(sketch, "E874", {"start": v(30.9, 182.8) * mm, "end": v(30.9, 178.04) * mm});
            skLineSegment(sketch, "E875", {"start": v(30.9, 178.04) * mm, "end": v(43.25, 178.04) * mm});
            skLineSegment(sketch, "E876", {"start": v(43.25, 182.8) * mm, "end": v(43.25, 178.04) * mm});
            skLineSegment(sketch, "E877", {"start": v(43.25, 182.8) * mm, "end": v(55.6, 182.8) * mm});
            skLineSegment(sketch, "E878", {"start": v(55.6, 182.8) * mm, "end": v(55.6, 178.04) * mm});
            skLineSegment(sketch, "E879", {"start": v(55.6, 178.04) * mm, "end": v(67.96, 178.04) * mm});
            skLineSegment(sketch, "E880", {"start": v(67.96, 182.8) * mm, "end": v(67.96, 178.04) * mm});
            skLineSegment(sketch, "E881", {"start": v(67.96, 182.8) * mm, "end": v(80.32, 182.8) * mm});
            skLineSegment(sketch, "E882", {"start": v(80.32, 182.8) * mm, "end": v(80.32, 178.04) * mm});
            skLineSegment(sketch, "E883", {"start": v(80.32, 178.04) * mm, "end": v(92.67, 178.04) * mm});
            skLineSegment(sketch, "E884", {"start": v(92.67, 182.8) * mm, "end": v(92.67, 178.04) * mm});
            skLineSegment(sketch, "E885", {"start": v(92.67, 182.8) * mm, "end": v(105.03, 182.8) * mm});
            skLineSegment(sketch, "E886", {"start": v(105.03, 182.8) * mm, "end": v(105.03, 178.04) * mm});
            skLineSegment(sketch, "E887", {"start": v(105.03, 178.04) * mm, "end": v(117.39, 178.04) * mm});
            skLineSegment(sketch, "E888", {"start": v(117.39, 182.8) * mm, "end": v(117.39, 178.04) * mm});
            skLineSegment(sketch, "E889", {"start": v(117.39, 182.8) * mm, "end": v(129.75, 182.8) * mm});
            skLineSegment(sketch, "E890", {"start": v(129.75, 182.8) * mm, "end": v(129.75, 178.04) * mm});
            skLineSegment(sketch, "E891", {"start": v(129.75, 178.04) * mm, "end": v(142.1, 178.04) * mm});
            skLineSegment(sketch, "E892", {"start": v(142.1, 182.8) * mm, "end": v(142.1, 178.04) * mm});
            skLineSegment(sketch, "E893", {"start": v(142.1, 182.8) * mm, "end": v(154.46, 182.8) * mm});
            skLineSegment(sketch, "E894", {"start": v(154.46, 182.8) * mm, "end": v(154.46, 178.04) * mm});
            skLineSegment(sketch, "E895", {"start": v(154.46, 178.04) * mm, "end": v(166.82, 178.04) * mm});
            skLineSegment(sketch, "E896", {"start": v(166.82, 182.8) * mm, "end": v(166.82, 178.04) * mm});
            skLineSegment(sketch, "E897", {"start": v(166.82, 182.8) * mm, "end": v(179.17, 182.8) * mm});
            skLineSegment(sketch, "E898", {"start": v(179.17, 182.8) * mm, "end": v(179.17, 178.04) * mm});
            skLineSegment(sketch, "E899", {"start": v(179.17, 178.04) * mm, "end": v(191.53, 178.04) * mm});
            skLineSegment(sketch, "E900", {"start": v(191.53, 182.8) * mm, "end": v(191.53, 178.04) * mm});
            skLineSegment(sketch, "E901", {"start": v(191.53, 182.8) * mm, "end": v(203.89, 182.8) * mm});
            skLineSegment(sketch, "E902", {"start": v(203.89, 182.8) * mm, "end": v(203.89, 178.04) * mm});
            skLineSegment(sketch, "E903", {"start": v(203.89, 178.04) * mm, "end": v(216.25, 178.04) * mm});
            skLineSegment(sketch, "E904", {"start": v(216.25, 182.8) * mm, "end": v(216.25, 178.04) * mm});
            skLineSegment(sketch, "E905", {"start": v(216.25, 182.8) * mm, "end": v(223.84, 182.8) * mm});
            skLineSegment(sketch, "E906", {"start": v(-228.6, 5) * mm, "end": v(-228.6, 16.85) * mm});
            skLineSegment(sketch, "E907", {"start": v(-223.84, 16.85) * mm, "end": v(-228.6, 16.85) * mm});
            skLineSegment(sketch, "E908", {"start": v(-223.84, 16.85) * mm, "end": v(-223.84, 28.7) * mm});
            skLineSegment(sketch, "E909", {"start": v(-223.84, 28.7) * mm, "end": v(-228.6, 28.7) * mm});
            skLineSegment(sketch, "E910", {"start": v(-228.6, 28.7) * mm, "end": v(-228.6, 40.56) * mm});
            skLineSegment(sketch, "E911", {"start": v(-223.84, 40.56) * mm, "end": v(-228.6, 40.56) * mm});
            skLineSegment(sketch, "E912", {"start": v(-223.84, 40.56) * mm, "end": v(-223.84, 52.41) * mm});
            skLineSegment(sketch, "E913", {"start": v(-223.84, 52.41) * mm, "end": v(-228.6, 52.41) * mm});
            skLineSegment(sketch, "E914", {"start": v(-228.6, 52.41) * mm, "end": v(-228.6, 64.26) * mm});
            skLineSegment(sketch, "E915", {"start": v(-223.84, 64.26) * mm, "end": v(-228.6, 64.26) * mm});
            skLineSegment(sketch, "E916", {"start": v(-223.84, 64.26) * mm, "end": v(-223.84, 76.12) * mm});
            skLineSegment(sketch, "E917", {"start": v(-223.84, 76.12) * mm, "end": v(-228.6, 76.12) * mm});
            skLineSegment(sketch, "E918", {"start": v(-228.6, 76.12) * mm, "end": v(-228.6, 87.97) * mm});
            skLineSegment(sketch, "E919", {"start": v(-223.84, 87.97) * mm, "end": v(-228.6, 87.97) * mm});
            skLineSegment(sketch, "E920", {"start": v(-223.84, 87.97) * mm, "end": v(-223.84, 99.82) * mm});
            skLineSegment(sketch, "E921", {"start": v(-223.84, 99.82) * mm, "end": v(-228.6, 99.82) * mm});
            skLineSegment(sketch, "E922", {"start": v(-228.6, 99.82) * mm, "end": v(-228.6, 111.68) * mm});
            skLineSegment(sketch, "E923", {"start": v(-223.84, 111.68) * mm, "end": v(-228.6, 111.68) * mm});
            skLineSegment(sketch, "E924", {"start": v(-223.84, 111.68) * mm, "end": v(-223.84, 123.53) * mm});
            skLineSegment(sketch, "E925", {"start": v(-223.84, 123.53) * mm, "end": v(-228.6, 123.53) * mm});
            skLineSegment(sketch, "E926", {"start": v(-228.6, 123.53) * mm, "end": v(-228.6, 135.38) * mm});
            skLineSegment(sketch, "E927", {"start": v(-223.84, 135.38) * mm, "end": v(-228.6, 135.38) * mm});
            skLineSegment(sketch, "E928", {"start": v(-223.84, 135.38) * mm, "end": v(-223.84, 147.24) * mm});
            skLineSegment(sketch, "E929", {"start": v(-223.84, 147.24) * mm, "end": v(-228.6, 147.24) * mm});
            skLineSegment(sketch, "E930", {"start": v(-228.6, 147.24) * mm, "end": v(-228.6, 159.1) * mm});
            skLineSegment(sketch, "E931", {"start": v(-223.84, 159.1) * mm, "end": v(-228.6, 159.1) * mm});
            skLineSegment(sketch, "E932", {"start": v(-223.84, 159.1) * mm, "end": v(-223.84, 170.94) * mm});
            skLineSegment(sketch, "E933", {"start": v(-223.84, 170.94) * mm, "end": v(-228.6, 170.94) * mm});
            skLineSegment(sketch, "E934", {"start": v(-228.6, 170.94) * mm, "end": v(-228.6, 182.8) * mm});
            skLineSegment(sketch, "E935", {"start": v(223.84, 5) * mm, "end": v(223.84, 16.85) * mm});
            skLineSegment(sketch, "E936", {"start": v(228.6, 16.85) * mm, "end": v(223.84, 16.85) * mm});
            skLineSegment(sketch, "E937", {"start": v(228.6, 16.85) * mm, "end": v(228.6, 28.7) * mm});
            skLineSegment(sketch, "E938", {"start": v(228.6, 28.7) * mm, "end": v(223.84, 28.7) * mm});
            skLineSegment(sketch, "E939", {"start": v(223.84, 28.7) * mm, "end": v(223.84, 40.56) * mm});
            skLineSegment(sketch, "E940", {"start": v(228.6, 40.56) * mm, "end": v(223.84, 40.56) * mm});
            skLineSegment(sketch, "E941", {"start": v(228.6, 40.56) * mm, "end": v(228.6, 52.41) * mm});
            skLineSegment(sketch, "E942", {"start": v(228.6, 52.41) * mm, "end": v(223.84, 52.41) * mm});
            skLineSegment(sketch, "E943", {"start": v(223.84, 52.41) * mm, "end": v(223.84, 64.26) * mm});
            skLineSegment(sketch, "E944", {"start": v(228.6, 64.26) * mm, "end": v(223.84, 64.26) * mm});
            skLineSegment(sketch, "E945", {"start": v(228.6, 64.26) * mm, "end": v(228.6, 76.12) * mm});
            skLineSegment(sketch, "E946", {"start": v(228.6, 76.12) * mm, "end": v(223.84, 76.12) * mm});
            skLineSegment(sketch, "E947", {"start": v(223.84, 76.12) * mm, "end": v(223.84, 87.97) * mm});
            skLineSegment(sketch, "E948", {"start": v(228.6, 87.97) * mm, "end": v(223.84, 87.97) * mm});
            skLineSegment(sketch, "E949", {"start": v(228.6, 87.97) * mm, "end": v(228.6, 99.82) * mm});
            skLineSegment(sketch, "E950", {"start": v(228.6, 99.82) * mm, "end": v(223.84, 99.82) * mm});
            skLineSegment(sketch, "E951", {"start": v(223.84, 99.82) * mm, "end": v(223.84, 111.68) * mm});
            skLineSegment(sketch, "E952", {"start": v(228.6, 111.68) * mm, "end": v(223.84, 111.68) * mm});
            skLineSegment(sketch, "E953", {"start": v(228.6, 111.68) * mm, "end": v(228.6, 123.53) * mm});
            skLineSegment(sketch, "E954", {"start": v(228.6, 123.53) * mm, "end": v(223.84, 123.53) * mm});
            skLineSegment(sketch, "E955", {"start": v(223.84, 123.53) * mm, "end": v(223.84, 135.38) * mm});
            skLineSegment(sketch, "E956", {"start": v(228.6, 135.38) * mm, "end": v(223.84, 135.38) * mm});
            skLineSegment(sketch, "E957", {"start": v(228.6, 135.38) * mm, "end": v(228.6, 147.24) * mm});
            skLineSegment(sketch, "E958", {"start": v(228.6, 147.24) * mm, "end": v(223.84, 147.24) * mm});
            skLineSegment(sketch, "E959", {"start": v(223.84, 147.24) * mm, "end": v(223.84, 159.1) * mm});
            skLineSegment(sketch, "E960", {"start": v(228.6, 159.1) * mm, "end": v(223.84, 159.1) * mm});
            skLineSegment(sketch, "E961", {"start": v(228.6, 159.1) * mm, "end": v(228.6, 170.94) * mm});
            skLineSegment(sketch, "E962", {"start": v(228.6, 170.94) * mm, "end": v(223.84, 170.94) * mm});
            skLineSegment(sketch, "E963", {"start": v(223.84, 170.94) * mm, "end": v(223.84, 182.8) * mm});
            skLineSegment(sketch, "E964", {"start": v(-223.84, 197.56) * mm, "end": v(-216.24, 197.56) * mm});
            skLineSegment(sketch, "E965", {"start": v(-216.24, 197.56) * mm, "end": v(-216.24, 192.8) * mm});
            skLineSegment(sketch, "E966", {"start": v(-216.24, 192.8) * mm, "end": v(-203.89, 192.8) * mm});
            skLineSegment(sketch, "E967", {"start": v(-203.89, 197.56) * mm, "end": v(-203.89, 192.8) * mm});
            skLineSegment(sketch, "E968", {"start": v(-203.89, 197.56) * mm, "end": v(-191.53, 197.56) * mm});
            skLineSegment(sketch, "E969", {"start": v(-191.53, 197.56) * mm, "end": v(-191.53, 192.8) * mm});
            skLineSegment(sketch, "E970", {"start": v(-191.53, 192.8) * mm, "end": v(-179.17, 192.8) * mm});
            skLineSegment(sketch, "E971", {"start": v(-179.17, 197.56) * mm, "end": v(-179.17, 192.8) * mm});
            skLineSegment(sketch, "E972", {"start": v(-179.17, 197.56) * mm, "end": v(-166.81, 197.56) * mm});
            skLineSegment(sketch, "E973", {"start": v(-166.81, 197.56) * mm, "end": v(-166.81, 192.8) * mm});
            skLineSegment(sketch, "E974", {"start": v(-166.81, 192.8) * mm, "end": v(-154.46, 192.8) * mm});
            skLineSegment(sketch, "E975", {"start": v(-154.46, 197.56) * mm, "end": v(-154.46, 192.8) * mm});
            skLineSegment(sketch, "E976", {"start": v(-154.46, 197.56) * mm, "end": v(-142.1, 197.56) * mm});
            skLineSegment(sketch, "E977", {"start": v(-142.1, 197.56) * mm, "end": v(-142.1, 192.8) * mm});
            skLineSegment(sketch, "E978", {"start": v(-142.1, 192.8) * mm, "end": v(-129.75, 192.8) * mm});
            skLineSegment(sketch, "E979", {"start": v(-129.75, 197.56) * mm, "end": v(-129.75, 192.8) * mm});
            skLineSegment(sketch, "E980", {"start": v(-129.75, 197.56) * mm, "end": v(-117.39, 197.56) * mm});
            skLineSegment(sketch, "E981", {"start": v(-117.39, 197.56) * mm, "end": v(-117.39, 192.8) * mm});
            skLineSegment(sketch, "E982", {"start": v(-117.39, 192.8) * mm, "end": v(-105.03, 192.8) * mm});
            skLineSegment(sketch, "E983", {"start": v(-105.03, 197.56) * mm, "end": v(-105.03, 192.8) * mm});
            skLineSegment(sketch, "E984", {"start": v(-105.03, 197.56) * mm, "end": v(-92.68, 197.56) * mm});
            skLineSegment(sketch, "E985", {"start": v(-92.68, 197.56) * mm, "end": v(-92.68, 192.8) * mm});
            skLineSegment(sketch, "E986", {"start": v(-92.68, 192.8) * mm, "end": v(-80.32, 192.8) * mm});
            skLineSegment(sketch, "E987", {"start": v(-80.32, 197.56) * mm, "end": v(-80.32, 192.8) * mm});
            skLineSegment(sketch, "E988", {"start": v(-80.32, 197.56) * mm, "end": v(-67.96, 197.56) * mm});
            skLineSegment(sketch, "E989", {"start": v(-67.96, 197.56) * mm, "end": v(-67.96, 192.8) * mm});
            skLineSegment(sketch, "E990", {"start": v(-67.96, 192.8) * mm, "end": v(-55.6, 192.8) * mm});
            skLineSegment(sketch, "E991", {"start": v(-55.6, 197.56) * mm, "end": v(-55.6, 192.8) * mm});
            skLineSegment(sketch, "E992", {"start": v(-55.6, 197.56) * mm, "end": v(-43.25, 197.56) * mm});
            skLineSegment(sketch, "E993", {"start": v(-43.25, 197.56) * mm, "end": v(-43.25, 192.8) * mm});
            skLineSegment(sketch, "E994", {"start": v(-43.25, 192.8) * mm, "end": v(-30.89, 192.8) * mm});
            skLineSegment(sketch, "E995", {"start": v(-30.89, 197.56) * mm, "end": v(-30.89, 192.8) * mm});
            skLineSegment(sketch, "E996", {"start": v(-30.89, 197.56) * mm, "end": v(-18.54, 197.56) * mm});
            skLineSegment(sketch, "E997", {"start": v(-18.54, 197.56) * mm, "end": v(-18.54, 192.8) * mm});
            skLineSegment(sketch, "E998", {"start": v(-18.54, 192.8) * mm, "end": v(-6.18, 192.8) * mm});
            skLineSegment(sketch, "E999", {"start": v(-6.18, 197.56) * mm, "end": v(-6.18, 192.8) * mm});
            skLineSegment(sketch, "E1000", {"start": v(-6.18, 197.56) * mm, "end": v(6.18, 197.56) * mm});
            skLineSegment(sketch, "E1001", {"start": v(6.18, 197.56) * mm, "end": v(6.18, 192.8) * mm});
            skLineSegment(sketch, "E1002", {"start": v(6.18, 192.8) * mm, "end": v(18.53, 192.8) * mm});
            skLineSegment(sketch, "E1003", {"start": v(18.53, 197.56) * mm, "end": v(18.53, 192.8) * mm});
            skLineSegment(sketch, "E1004", {"start": v(18.53, 197.56) * mm, "end": v(30.9, 197.56) * mm});
            skLineSegment(sketch, "E1005", {"start": v(30.9, 197.56) * mm, "end": v(30.9, 192.8) * mm});
            skLineSegment(sketch, "E1006", {"start": v(30.9, 192.8) * mm, "end": v(43.25, 192.8) * mm});
            skLineSegment(sketch, "E1007", {"start": v(43.25, 197.56) * mm, "end": v(43.25, 192.8) * mm});
            skLineSegment(sketch, "E1008", {"start": v(43.25, 197.56) * mm, "end": v(55.6, 197.56) * mm});
            skLineSegment(sketch, "E1009", {"start": v(55.6, 197.56) * mm, "end": v(55.6, 192.8) * mm});
            skLineSegment(sketch, "E1010", {"start": v(55.6, 192.8) * mm, "end": v(67.96, 192.8) * mm});
            skLineSegment(sketch, "E1011", {"start": v(67.96, 197.56) * mm, "end": v(67.96, 192.8) * mm});
            skLineSegment(sketch, "E1012", {"start": v(67.96, 197.56) * mm, "end": v(80.32, 197.56) * mm});
            skLineSegment(sketch, "E1013", {"start": v(80.32, 197.56) * mm, "end": v(80.32, 192.8) * mm});
            skLineSegment(sketch, "E1014", {"start": v(80.32, 192.8) * mm, "end": v(92.67, 192.8) * mm});
            skLineSegment(sketch, "E1015", {"start": v(92.67, 197.56) * mm, "end": v(92.67, 192.8) * mm});
            skLineSegment(sketch, "E1016", {"start": v(92.67, 197.56) * mm, "end": v(105.03, 197.56) * mm});
            skLineSegment(sketch, "E1017", {"start": v(105.03, 197.56) * mm, "end": v(105.03, 192.8) * mm});
            skLineSegment(sketch, "E1018", {"start": v(105.03, 192.8) * mm, "end": v(117.39, 192.8) * mm});
            skLineSegment(sketch, "E1019", {"start": v(117.39, 197.56) * mm, "end": v(117.39, 192.8) * mm});
            skLineSegment(sketch, "E1020", {"start": v(117.39, 197.56) * mm, "end": v(129.75, 197.56) * mm});
            skLineSegment(sketch, "E1021", {"start": v(129.75, 197.56) * mm, "end": v(129.75, 192.8) * mm});
            skLineSegment(sketch, "E1022", {"start": v(129.75, 192.8) * mm, "end": v(142.1, 192.8) * mm});
            skLineSegment(sketch, "E1023", {"start": v(142.1, 197.56) * mm, "end": v(142.1, 192.8) * mm});
            skLineSegment(sketch, "E1024", {"start": v(142.1, 197.56) * mm, "end": v(154.46, 197.56) * mm});
            skLineSegment(sketch, "E1025", {"start": v(154.46, 197.56) * mm, "end": v(154.46, 192.8) * mm});
            skLineSegment(sketch, "E1026", {"start": v(154.46, 192.8) * mm, "end": v(166.82, 192.8) * mm});
            skLineSegment(sketch, "E1027", {"start": v(166.82, 197.56) * mm, "end": v(166.82, 192.8) * mm});
            skLineSegment(sketch, "E1028", {"start": v(166.82, 197.56) * mm, "end": v(179.17, 197.56) * mm});
            skLineSegment(sketch, "E1029", {"start": v(179.17, 197.56) * mm, "end": v(179.17, 192.8) * mm});
            skLineSegment(sketch, "E1030", {"start": v(179.17, 192.8) * mm, "end": v(191.53, 192.8) * mm});
            skLineSegment(sketch, "E1031", {"start": v(191.53, 197.56) * mm, "end": v(191.53, 192.8) * mm});
            skLineSegment(sketch, "E1032", {"start": v(191.53, 197.56) * mm, "end": v(203.89, 197.56) * mm});
            skLineSegment(sketch, "E1033", {"start": v(203.89, 197.56) * mm, "end": v(203.89, 192.8) * mm});
            skLineSegment(sketch, "E1034", {"start": v(203.89, 192.8) * mm, "end": v(216.25, 192.8) * mm});
            skLineSegment(sketch, "E1035", {"start": v(216.25, 197.56) * mm, "end": v(216.25, 192.8) * mm});
            skLineSegment(sketch, "E1036", {"start": v(216.25, 197.56) * mm, "end": v(223.84, 197.56) * mm});
            skLineSegment(sketch, "E1037", {"start": v(-223.84, 492.84) * mm, "end": v(-216.24, 492.84) * mm});
            skLineSegment(sketch, "E1038", {"start": v(-216.24, 497.6) * mm, "end": v(-216.24, 492.84) * mm});
            skLineSegment(sketch, "E1039", {"start": v(-216.24, 497.6) * mm, "end": v(-203.89, 497.6) * mm});
            skLineSegment(sketch, "E1040", {"start": v(-203.89, 497.6) * mm, "end": v(-203.89, 492.84) * mm});
            skLineSegment(sketch, "E1041", {"start": v(-203.89, 492.84) * mm, "end": v(-191.53, 492.84) * mm});
            skLineSegment(sketch, "E1042", {"start": v(-191.53, 497.6) * mm, "end": v(-191.53, 492.84) * mm});
            skLineSegment(sketch, "E1043", {"start": v(-191.53, 497.6) * mm, "end": v(-179.17, 497.6) * mm});
            skLineSegment(sketch, "E1044", {"start": v(-179.17, 497.6) * mm, "end": v(-179.17, 492.84) * mm});
            skLineSegment(sketch, "E1045", {"start": v(-179.17, 492.84) * mm, "end": v(-166.81, 492.84) * mm});
            skLineSegment(sketch, "E1046", {"start": v(-166.81, 497.6) * mm, "end": v(-166.81, 492.84) * mm});
            skLineSegment(sketch, "E1047", {"start": v(-166.81, 497.6) * mm, "end": v(-154.46, 497.6) * mm});
            skLineSegment(sketch, "E1048", {"start": v(-154.46, 497.6) * mm, "end": v(-154.46, 492.84) * mm});
            skLineSegment(sketch, "E1049", {"start": v(-154.46, 492.84) * mm, "end": v(-142.1, 492.84) * mm});
            skLineSegment(sketch, "E1050", {"start": v(-142.1, 497.6) * mm, "end": v(-142.1, 492.84) * mm});
            skLineSegment(sketch, "E1051", {"start": v(-142.1, 497.6) * mm, "end": v(-129.75, 497.6) * mm});
            skLineSegment(sketch, "E1052", {"start": v(-129.75, 497.6) * mm, "end": v(-129.75, 492.84) * mm});
            skLineSegment(sketch, "E1053", {"start": v(-129.75, 492.84) * mm, "end": v(-117.39, 492.84) * mm});
            skLineSegment(sketch, "E1054", {"start": v(-117.39, 497.6) * mm, "end": v(-117.39, 492.84) * mm});
            skLineSegment(sketch, "E1055", {"start": v(-117.39, 497.6) * mm, "end": v(-105.03, 497.6) * mm});
            skLineSegment(sketch, "E1056", {"start": v(-105.03, 497.6) * mm, "end": v(-105.03, 492.84) * mm});
            skLineSegment(sketch, "E1057", {"start": v(-105.03, 492.84) * mm, "end": v(-92.68, 492.84) * mm});
            skLineSegment(sketch, "E1058", {"start": v(-92.68, 497.6) * mm, "end": v(-92.68, 492.84) * mm});
            skLineSegment(sketch, "E1059", {"start": v(-92.68, 497.6) * mm, "end": v(-80.32, 497.6) * mm});
            skLineSegment(sketch, "E1060", {"start": v(-80.32, 497.6) * mm, "end": v(-80.32, 492.84) * mm});
            skLineSegment(sketch, "E1061", {"start": v(-80.32, 492.84) * mm, "end": v(-67.96, 492.84) * mm});
            skLineSegment(sketch, "E1062", {"start": v(-67.96, 497.6) * mm, "end": v(-67.96, 492.84) * mm});
            skLineSegment(sketch, "E1063", {"start": v(-67.96, 497.6) * mm, "end": v(-55.6, 497.6) * mm});
            skLineSegment(sketch, "E1064", {"start": v(-55.6, 497.6) * mm, "end": v(-55.6, 492.84) * mm});
            skLineSegment(sketch, "E1065", {"start": v(-55.6, 492.84) * mm, "end": v(-43.25, 492.84) * mm});
            skLineSegment(sketch, "E1066", {"start": v(-43.25, 497.6) * mm, "end": v(-43.25, 492.84) * mm});
            skLineSegment(sketch, "E1067", {"start": v(-43.25, 497.6) * mm, "end": v(-30.89, 497.6) * mm});
            skLineSegment(sketch, "E1068", {"start": v(-30.89, 497.6) * mm, "end": v(-30.89, 492.84) * mm});
            skLineSegment(sketch, "E1069", {"start": v(-30.89, 492.84) * mm, "end": v(-18.54, 492.84) * mm});
            skLineSegment(sketch, "E1070", {"start": v(-18.54, 497.6) * mm, "end": v(-18.54, 492.84) * mm});
            skLineSegment(sketch, "E1071", {"start": v(-18.54, 497.6) * mm, "end": v(-6.18, 497.6) * mm});
            skLineSegment(sketch, "E1072", {"start": v(-6.18, 497.6) * mm, "end": v(-6.18, 492.84) * mm});
            skLineSegment(sketch, "E1073", {"start": v(-6.18, 492.84) * mm, "end": v(6.18, 492.84) * mm});
            skLineSegment(sketch, "E1074", {"start": v(6.18, 497.6) * mm, "end": v(6.18, 492.84) * mm});
            skLineSegment(sketch, "E1075", {"start": v(6.18, 497.6) * mm, "end": v(18.53, 497.6) * mm});
            skLineSegment(sketch, "E1076", {"start": v(18.53, 497.6) * mm, "end": v(18.53, 492.84) * mm});
            skLineSegment(sketch, "E1077", {"start": v(18.53, 492.84) * mm, "end": v(30.9, 492.84) * mm});
            skLineSegment(sketch, "E1078", {"start": v(30.9, 497.6) * mm, "end": v(30.9, 492.84) * mm});
            skLineSegment(sketch, "E1079", {"start": v(30.9, 497.6) * mm, "end": v(43.25, 497.6) * mm});
            skLineSegment(sketch, "E1080", {"start": v(43.25, 497.6) * mm, "end": v(43.25, 492.84) * mm});
            skLineSegment(sketch, "E1081", {"start": v(43.25, 492.84) * mm, "end": v(55.6, 492.84) * mm});
            skLineSegment(sketch, "E1082", {"start": v(55.6, 497.6) * mm, "end": v(55.6, 492.84) * mm});
            skLineSegment(sketch, "E1083", {"start": v(55.6, 497.6) * mm, "end": v(67.96, 497.6) * mm});
            skLineSegment(sketch, "E1084", {"start": v(67.96, 497.6) * mm, "end": v(67.96, 492.84) * mm});
            skLineSegment(sketch, "E1085", {"start": v(67.96, 492.84) * mm, "end": v(80.32, 492.84) * mm});
            skLineSegment(sketch, "E1086", {"start": v(80.32, 497.6) * mm, "end": v(80.32, 492.84) * mm});
            skLineSegment(sketch, "E1087", {"start": v(80.32, 497.6) * mm, "end": v(92.67, 497.6) * mm});
            skLineSegment(sketch, "E1088", {"start": v(92.67, 497.6) * mm, "end": v(92.67, 492.84) * mm});
            skLineSegment(sketch, "E1089", {"start": v(92.67, 492.84) * mm, "end": v(105.03, 492.84) * mm});
            skLineSegment(sketch, "E1090", {"start": v(105.03, 497.6) * mm, "end": v(105.03, 492.84) * mm});
            skLineSegment(sketch, "E1091", {"start": v(105.03, 497.6) * mm, "end": v(117.39, 497.6) * mm});
            skLineSegment(sketch, "E1092", {"start": v(117.39, 497.6) * mm, "end": v(117.39, 492.84) * mm});
            skLineSegment(sketch, "E1093", {"start": v(117.39, 492.84) * mm, "end": v(129.75, 492.84) * mm});
            skLineSegment(sketch, "E1094", {"start": v(129.75, 497.6) * mm, "end": v(129.75, 492.84) * mm});
            skLineSegment(sketch, "E1095", {"start": v(129.75, 497.6) * mm, "end": v(142.1, 497.6) * mm});
            skLineSegment(sketch, "E1096", {"start": v(142.1, 497.6) * mm, "end": v(142.1, 492.84) * mm});
            skLineSegment(sketch, "E1097", {"start": v(142.1, 492.84) * mm, "end": v(154.46, 492.84) * mm});
            skLineSegment(sketch, "E1098", {"start": v(154.46, 497.6) * mm, "end": v(154.46, 492.84) * mm});
            skLineSegment(sketch, "E1099", {"start": v(154.46, 497.6) * mm, "end": v(166.82, 497.6) * mm});
            skLineSegment(sketch, "E1100", {"start": v(166.82, 497.6) * mm, "end": v(166.82, 492.84) * mm});
            skLineSegment(sketch, "E1101", {"start": v(166.82, 492.84) * mm, "end": v(179.17, 492.84) * mm});
            skLineSegment(sketch, "E1102", {"start": v(179.17, 497.6) * mm, "end": v(179.17, 492.84) * mm});
            skLineSegment(sketch, "E1103", {"start": v(179.17, 497.6) * mm, "end": v(191.53, 497.6) * mm});
            skLineSegment(sketch, "E1104", {"start": v(191.53, 497.6) * mm, "end": v(191.53, 492.84) * mm});
            skLineSegment(sketch, "E1105", {"start": v(191.53, 492.84) * mm, "end": v(203.89, 492.84) * mm});
            skLineSegment(sketch, "E1106", {"start": v(203.89, 497.6) * mm, "end": v(203.89, 492.84) * mm});
            skLineSegment(sketch, "E1107", {"start": v(203.89, 497.6) * mm, "end": v(216.25, 497.6) * mm});
            skLineSegment(sketch, "E1108", {"start": v(216.25, 497.6) * mm, "end": v(216.25, 492.84) * mm});
            skLineSegment(sketch, "E1109", {"start": v(216.25, 492.84) * mm, "end": v(223.84, 492.84) * mm});
            skLineSegment(sketch, "E1110", {"start": v(-223.84, 197.56) * mm, "end": v(-223.84, 205) * mm});
            skLineSegment(sketch, "E1111", {"start": v(-223.84, 205) * mm, "end": v(-228.6, 205) * mm});
            skLineSegment(sketch, "E1112", {"start": v(-228.6, 205) * mm, "end": v(-228.6, 217.19) * mm});
            skLineSegment(sketch, "E1113", {"start": v(-223.84, 217.19) * mm, "end": v(-228.6, 217.19) * mm});
            skLineSegment(sketch, "E1114", {"start": v(-223.84, 217.19) * mm, "end": v(-223.84, 229.38) * mm});
            skLineSegment(sketch, "E1115", {"start": v(-223.84, 229.38) * mm, "end": v(-228.6, 229.38) * mm});
            skLineSegment(sketch, "E1116", {"start": v(-228.6, 229.38) * mm, "end": v(-228.6, 241.57) * mm});
            skLineSegment(sketch, "E1117", {"start": v(-223.84, 241.57) * mm, "end": v(-228.6, 241.57) * mm});
            skLineSegment(sketch, "E1118", {"start": v(-223.84, 241.57) * mm, "end": v(-223.84, 253.76) * mm});
            skLineSegment(sketch, "E1119", {"start": v(-223.84, 253.76) * mm, "end": v(-228.6, 253.76) * mm});
            skLineSegment(sketch, "E1120", {"start": v(-228.6, 253.76) * mm, "end": v(-228.6, 265.95) * mm});
            skLineSegment(sketch, "E1121", {"start": v(-223.84, 265.95) * mm, "end": v(-228.6, 265.95) * mm});
            skLineSegment(sketch, "E1122", {"start": v(-223.84, 265.95) * mm, "end": v(-223.84, 278.14) * mm});
            skLineSegment(sketch, "E1123", {"start": v(-223.84, 278.14) * mm, "end": v(-228.6, 278.14) * mm});
            skLineSegment(sketch, "E1124", {"start": v(-228.6, 278.14) * mm, "end": v(-228.6, 290.34) * mm});
            skLineSegment(sketch, "E1125", {"start": v(-223.84, 290.34) * mm, "end": v(-228.6, 290.34) * mm});
            skLineSegment(sketch, "E1126", {"start": v(-223.84, 290.34) * mm, "end": v(-223.84, 302.53) * mm});
            skLineSegment(sketch, "E1127", {"start": v(-223.84, 302.53) * mm, "end": v(-228.6, 302.53) * mm});
            skLineSegment(sketch, "E1128", {"start": v(-228.6, 302.53) * mm, "end": v(-228.6, 314.72) * mm});
            skLineSegment(sketch, "E1129", {"start": v(-223.84, 314.72) * mm, "end": v(-228.6, 314.72) * mm});
            skLineSegment(sketch, "E1130", {"start": v(-223.84, 314.72) * mm, "end": v(-223.84, 326.91) * mm});
            skLineSegment(sketch, "E1131", {"start": v(-223.84, 326.91) * mm, "end": v(-228.6, 326.91) * mm});
            skLineSegment(sketch, "E1132", {"start": v(-228.6, 326.91) * mm, "end": v(-228.6, 339.1) * mm});
            skLineSegment(sketch, "E1133", {"start": v(-223.84, 339.1) * mm, "end": v(-228.6, 339.1) * mm});
            skLineSegment(sketch, "E1134", {"start": v(-223.84, 339.1) * mm, "end": v(-223.84, 351.3) * mm});
            skLineSegment(sketch, "E1135", {"start": v(-223.84, 351.3) * mm, "end": v(-228.6, 351.3) * mm});
            skLineSegment(sketch, "E1136", {"start": v(-228.6, 351.3) * mm, "end": v(-228.6, 363.49) * mm});
            skLineSegment(sketch, "E1137", {"start": v(-223.84, 363.49) * mm, "end": v(-228.6, 363.49) * mm});
            skLineSegment(sketch, "E1138", {"start": v(-223.84, 363.49) * mm, "end": v(-223.84, 375.68) * mm});
            skLineSegment(sketch, "E1139", {"start": v(-223.84, 375.68) * mm, "end": v(-228.6, 375.68) * mm});
            skLineSegment(sketch, "E1140", {"start": v(-228.6, 375.68) * mm, "end": v(-228.6, 387.87) * mm});
            skLineSegment(sketch, "E1141", {"start": v(-223.84, 387.87) * mm, "end": v(-228.6, 387.87) * mm});
            skLineSegment(sketch, "E1142", {"start": v(-223.84, 387.87) * mm, "end": v(-223.84, 400.07) * mm});
            skLineSegment(sketch, "E1143", {"start": v(-223.84, 400.07) * mm, "end": v(-228.6, 400.07) * mm});
            skLineSegment(sketch, "E1144", {"start": v(-228.6, 400.07) * mm, "end": v(-228.6, 412.25) * mm});
            skLineSegment(sketch, "E1145", {"start": v(-223.84, 412.25) * mm, "end": v(-228.6, 412.25) * mm});
            skLineSegment(sketch, "E1146", {"start": v(-223.84, 412.25) * mm, "end": v(-223.84, 424.45) * mm});
            skLineSegment(sketch, "E1147", {"start": v(-223.84, 424.45) * mm, "end": v(-228.6, 424.45) * mm});
            skLineSegment(sketch, "E1148", {"start": v(-228.6, 424.45) * mm, "end": v(-228.6, 436.64) * mm});
            skLineSegment(sketch, "E1149", {"start": v(-223.84, 436.64) * mm, "end": v(-228.6, 436.64) * mm});
            skLineSegment(sketch, "E1150", {"start": v(-223.84, 436.64) * mm, "end": v(-223.84, 448.83) * mm});
            skLineSegment(sketch, "E1151", {"start": v(-223.84, 448.83) * mm, "end": v(-228.6, 448.83) * mm});
            skLineSegment(sketch, "E1152", {"start": v(-228.6, 448.83) * mm, "end": v(-228.6, 461.03) * mm});
            skLineSegment(sketch, "E1153", {"start": v(-223.84, 461.03) * mm, "end": v(-228.6, 461.03) * mm});
            skLineSegment(sketch, "E1154", {"start": v(-223.84, 461.03) * mm, "end": v(-223.84, 473.22) * mm});
            skLineSegment(sketch, "E1155", {"start": v(-223.84, 473.22) * mm, "end": v(-228.6, 473.22) * mm});
            skLineSegment(sketch, "E1156", {"start": v(-228.6, 473.22) * mm, "end": v(-228.6, 485.4) * mm});
            skLineSegment(sketch, "E1157", {"start": v(-223.84, 485.4) * mm, "end": v(-228.6, 485.4) * mm});
            skLineSegment(sketch, "E1158", {"start": v(-223.84, 485.4) * mm, "end": v(-223.84, 492.84) * mm});
            skLineSegment(sketch, "E1159", {"start": v(223.84, 197.56) * mm, "end": v(223.84, 205) * mm});
            skLineSegment(sketch, "E1160", {"start": v(228.6, 205) * mm, "end": v(223.84, 205) * mm});
            skLineSegment(sketch, "E1161", {"start": v(228.6, 205) * mm, "end": v(228.6, 217.19) * mm});
            skLineSegment(sketch, "E1162", {"start": v(228.6, 217.19) * mm, "end": v(223.84, 217.19) * mm});
            skLineSegment(sketch, "E1163", {"start": v(223.84, 217.19) * mm, "end": v(223.84, 229.38) * mm});
            skLineSegment(sketch, "E1164", {"start": v(228.6, 229.38) * mm, "end": v(223.84, 229.38) * mm});
            skLineSegment(sketch, "E1165", {"start": v(228.6, 229.38) * mm, "end": v(228.6, 241.57) * mm});
            skLineSegment(sketch, "E1166", {"start": v(228.6, 241.57) * mm, "end": v(223.84, 241.57) * mm});
            skLineSegment(sketch, "E1167", {"start": v(223.84, 241.57) * mm, "end": v(223.84, 253.76) * mm});
            skLineSegment(sketch, "E1168", {"start": v(228.6, 253.76) * mm, "end": v(223.84, 253.76) * mm});
            skLineSegment(sketch, "E1169", {"start": v(228.6, 253.76) * mm, "end": v(228.6, 265.95) * mm});
            skLineSegment(sketch, "E1170", {"start": v(228.6, 265.95) * mm, "end": v(223.84, 265.95) * mm});
            skLineSegment(sketch, "E1171", {"start": v(223.84, 265.95) * mm, "end": v(223.84, 278.14) * mm});
            skLineSegment(sketch, "E1172", {"start": v(228.6, 278.14) * mm, "end": v(223.84, 278.14) * mm});
            skLineSegment(sketch, "E1173", {"start": v(228.6, 278.14) * mm, "end": v(228.6, 290.34) * mm});
            skLineSegment(sketch, "E1174", {"start": v(228.6, 290.34) * mm, "end": v(223.84, 290.34) * mm});
            skLineSegment(sketch, "E1175", {"start": v(223.84, 290.34) * mm, "end": v(223.84, 302.53) * mm});
            skLineSegment(sketch, "E1176", {"start": v(228.6, 302.53) * mm, "end": v(223.84, 302.53) * mm});
            skLineSegment(sketch, "E1177", {"start": v(228.6, 302.53) * mm, "end": v(228.6, 314.72) * mm});
            skLineSegment(sketch, "E1178", {"start": v(228.6, 314.72) * mm, "end": v(223.84, 314.72) * mm});
            skLineSegment(sketch, "E1179", {"start": v(223.84, 314.72) * mm, "end": v(223.84, 326.91) * mm});
            skLineSegment(sketch, "E1180", {"start": v(228.6, 326.91) * mm, "end": v(223.84, 326.91) * mm});
            skLineSegment(sketch, "E1181", {"start": v(228.6, 326.91) * mm, "end": v(228.6, 339.1) * mm});
            skLineSegment(sketch, "E1182", {"start": v(228.6, 339.1) * mm, "end": v(223.84, 339.1) * mm});
            skLineSegment(sketch, "E1183", {"start": v(223.84, 339.1) * mm, "end": v(223.84, 351.3) * mm});
            skLineSegment(sketch, "E1184", {"start": v(228.6, 351.3) * mm, "end": v(223.84, 351.3) * mm});
            skLineSegment(sketch, "E1185", {"start": v(228.6, 351.3) * mm, "end": v(228.6, 363.49) * mm});
            skLineSegment(sketch, "E1186", {"start": v(228.6, 363.49) * mm, "end": v(223.84, 363.49) * mm});
            skLineSegment(sketch, "E1187", {"start": v(223.84, 363.49) * mm, "end": v(223.84, 375.68) * mm});
            skLineSegment(sketch, "E1188", {"start": v(228.6, 375.68) * mm, "end": v(223.84, 375.68) * mm});
            skLineSegment(sketch, "E1189", {"start": v(228.6, 375.68) * mm, "end": v(228.6, 387.87) * mm});
            skLineSegment(sketch, "E1190", {"start": v(228.6, 387.87) * mm, "end": v(223.84, 387.87) * mm});
            skLineSegment(sketch, "E1191", {"start": v(223.84, 387.87) * mm, "end": v(223.84, 400.07) * mm});
            skLineSegment(sketch, "E1192", {"start": v(228.6, 400.07) * mm, "end": v(223.84, 400.07) * mm});
            skLineSegment(sketch, "E1193", {"start": v(228.6, 400.07) * mm, "end": v(228.6, 412.25) * mm});
            skLineSegment(sketch, "E1194", {"start": v(228.6, 412.25) * mm, "end": v(223.84, 412.25) * mm});
            skLineSegment(sketch, "E1195", {"start": v(223.84, 412.25) * mm, "end": v(223.84, 424.45) * mm});
            skLineSegment(sketch, "E1196", {"start": v(228.6, 424.45) * mm, "end": v(223.84, 424.45) * mm});
            skLineSegment(sketch, "E1197", {"start": v(228.6, 424.45) * mm, "end": v(228.6, 436.64) * mm});
            skLineSegment(sketch, "E1198", {"start": v(228.6, 436.64) * mm, "end": v(223.84, 436.64) * mm});
            skLineSegment(sketch, "E1199", {"start": v(223.84, 436.64) * mm, "end": v(223.84, 448.83) * mm});
            skLineSegment(sketch, "E1200", {"start": v(228.6, 448.83) * mm, "end": v(223.84, 448.83) * mm});
            skLineSegment(sketch, "E1201", {"start": v(228.6, 448.83) * mm, "end": v(228.6, 461.03) * mm});
            skLineSegment(sketch, "E1202", {"start": v(228.6, 461.03) * mm, "end": v(223.84, 461.03) * mm});
            skLineSegment(sketch, "E1203", {"start": v(223.84, 461.03) * mm, "end": v(223.84, 473.22) * mm});
            skLineSegment(sketch, "E1204", {"start": v(228.6, 473.22) * mm, "end": v(223.84, 473.22) * mm});
            skLineSegment(sketch, "E1205", {"start": v(228.6, 473.22) * mm, "end": v(228.6, 485.4) * mm});
            skLineSegment(sketch, "E1206", {"start": v(228.6, 485.4) * mm, "end": v(223.84, 485.4) * mm});
            skLineSegment(sketch, "E1207", {"start": v(223.84, 485.4) * mm, "end": v(223.84, 492.84) * mm});
            skSolve(sketch);
        }
        {
            var Q0;
            Q0 = qSketchRegion(id + "F0", true);
            extrude(context, id + "F1", {"entities" : qUnion([Q0]), "depth" : 25.4 * mm});
        }
        {
            var Q0;
            Q0=makeQuery(id+"F1.opExtrude","CAP_FACE",FACE,{"disambiguationData":[OSD([sQuery(id+"F0.wireOp",EDGE,"E760"),sQuery(id+"F0.wireOp",EDGE,"E761"),sQuery(id+"F0.wireOp",EDGE,"E762"),sQuery(id+"F0.wireOp",EDGE,"E763"),sQuery(id+"F0.wireOp",EDGE,"E764"),sQuery(id+"F0.wireOp",EDGE,"E765"),sQuery(id+"F0.wireOp",EDGE,"E766"),sQuery(id+"F0.wireOp",EDGE,"E767"),sQuery(id+"F0.wireOp",EDGE,"E768"),sQuery(id+"F0.wireOp",EDGE,"E769"),sQuery(id+"F0.wireOp",EDGE,"E770"),sQuery(id+"F0.wireOp",EDGE,"E771"),sQuery(id+"F0.wireOp",EDGE,"E772"),sQuery(id+"F0.wireOp",EDGE,"E773"),sQuery(id+"F0.wireOp",EDGE,"E774"),sQuery(id+"F0.wireOp",EDGE,"E775"),sQuery(id+"F0.wireOp",EDGE,"E776"),sQuery(id+"F0.wireOp",EDGE,"E777"),sQuery(id+"F0.wireOp",EDGE,"E778"),sQuery(id+"F0.wireOp",EDGE,"E779"),sQuery(id+"F0.wireOp",EDGE,"E780"),sQuery(id+"F0.wireOp",EDGE,"E781"),sQuery(id+"F0.wireOp",EDGE,"E782"),sQuery(id+"F0.wireOp",EDGE,"E783"),sQuery(id+"F0.wireOp",EDGE,"E784"),sQuery(id+"F0.wireOp",EDGE,"E785"),sQuery(id+"F0.wireOp",EDGE,"E786"),sQuery(id+"F0.wireOp",EDGE,"E787"),sQuery(id+"F0.wireOp",EDGE,"E788"),sQuery(id+"F0.wireOp",EDGE,"E789"),sQuery(id+"F0.wireOp",EDGE,"E790"),sQuery(id+"F0.wireOp",EDGE,"E791"),sQuery(id+"F0.wireOp",EDGE,"E792"),sQuery(id+"F0.wireOp",EDGE,"E793"),sQuery(id+"F0.wireOp",EDGE,"E794"),sQuery(id+"F0.wireOp",EDGE,"E795"),sQuery(id+"F0.wireOp",EDGE,"E796"),sQuery(id+"F0.wireOp",EDGE,"E797"),sQuery(id+"F0.wireOp",EDGE,"E798"),sQuery(id+"F0.wireOp",EDGE,"E799"),sQuery(id+"F0.wireOp",EDGE,"E800"),sQuery(id+"F0.wireOp",EDGE,"E801"),sQuery(id+"F0.wireOp",EDGE,"E802"),sQuery(id+"F0.wireOp",EDGE,"E803"),sQuery(id+"F0.wireOp",EDGE,"E804"),sQuery(id+"F0.wireOp",EDGE,"E805"),sQuery(id+"F0.wireOp",EDGE,"E806"),sQuery(id+"F0.wireOp",EDGE,"E807"),sQuery(id+"F0.wireOp",EDGE,"E808"),sQuery(id+"F0.wireOp",EDGE,"E809"),sQuery(id+"F0.wireOp",EDGE,"E810"),sQuery(id+"F0.wireOp",EDGE,"E811"),sQuery(id+"F0.wireOp",EDGE,"E812"),sQuery(id+"F0.wireOp",EDGE,"E813"),sQuery(id+"F0.wireOp",EDGE,"E814"),sQuery(id+"F0.wireOp",EDGE,"E815"),sQuery(id+"F0.wireOp",EDGE,"E816"),sQuery(id+"F0.wireOp",EDGE,"E817"),sQuery(id+"F0.wireOp",EDGE,"E818"),sQuery(id+"F0.wireOp",EDGE,"E819"),sQuery(id+"F0.wireOp",EDGE,"E820"),sQuery(id+"F0.wireOp",EDGE,"E821"),sQuery(id+"F0.wireOp",EDGE,"E822"),sQuery(id+"F0.wireOp",EDGE,"E823"),sQuery(id+"F0.wireOp",EDGE,"E824"),sQuery(id+"F0.wireOp",EDGE,"E825"),sQuery(id+"F0.wireOp",EDGE,"E826"),sQuery(id+"F0.wireOp",EDGE,"E827"),sQuery(id+"F0.wireOp",EDGE,"E828"),sQuery(id+"F0.wireOp",EDGE,"E829"),sQuery(id+"F0.wireOp",EDGE,"E830"),sQuery(id+"F0.wireOp",EDGE,"E831"),sQuery(id+"F0.wireOp",EDGE,"E832"),sQuery(id+"F0.wireOp",EDGE,"E833"),sQuery(id+"F0.wireOp",EDGE,"E834"),sQuery(id+"F0.wireOp",EDGE,"E835"),sQuery(id+"F0.wireOp",EDGE,"E836"),sQuery(id+"F0.wireOp",EDGE,"E837"),sQuery(id+"F0.wireOp",EDGE,"E838"),sQuery(id+"F0.wireOp",EDGE,"E839"),sQuery(id+"F0.wireOp",EDGE,"E840"),sQuery(id+"F0.wireOp",EDGE,"E841"),sQuery(id+"F0.wireOp",EDGE,"E842"),sQuery(id+"F0.wireOp",EDGE,"E843"),sQuery(id+"F0.wireOp",EDGE,"E844"),sQuery(id+"F0.wireOp",EDGE,"E845"),sQuery(id+"F0.wireOp",EDGE,"E846"),sQuery(id+"F0.wireOp",EDGE,"E847"),sQuery(id+"F0.wireOp",EDGE,"E848"),sQuery(id+"F0.wireOp",EDGE,"E849"),sQuery(id+"F0.wireOp",EDGE,"E850"),sQuery(id+"F0.wireOp",EDGE,"E851"),sQuery(id+"F0.wireOp",EDGE,"E852"),sQuery(id+"F0.wireOp",EDGE,"E853"),sQuery(id+"F0.wireOp",EDGE,"E854"),sQuery(id+"F0.wireOp",EDGE,"E855"),sQuery(id+"F0.wireOp",EDGE,"E856"),sQuery(id+"F0.wireOp",EDGE,"E857"),sQuery(id+"F0.wireOp",EDGE,"E858"),sQuery(id+"F0.wireOp",EDGE,"E859"),sQuery(id+"F0.wireOp",EDGE,"E860"),sQuery(id+"F0.wireOp",EDGE,"E861"),sQuery(id+"F0.wireOp",EDGE,"E862"),sQuery(id+"F0.wireOp",EDGE,"E863"),sQuery(id+"F0.wireOp",EDGE,"E864"),sQuery(id+"F0.wireOp",EDGE,"E865"),sQuery(id+"F0.wireOp",EDGE,"E866"),sQuery(id+"F0.wireOp",EDGE,"E867"),sQuery(id+"F0.wireOp",EDGE,"E868"),sQuery(id+"F0.wireOp",EDGE,"E869"),sQuery(id+"F0.wireOp",EDGE,"E870"),sQuery(id+"F0.wireOp",EDGE,"E871"),sQuery(id+"F0.wireOp",EDGE,"E872"),sQuery(id+"F0.wireOp",EDGE,"E873"),sQuery(id+"F0.wireOp",EDGE,"E874"),sQuery(id+"F0.wireOp",EDGE,"E875"),sQuery(id+"F0.wireOp",EDGE,"E876"),sQuery(id+"F0.wireOp",EDGE,"E877"),sQuery(id+"F0.wireOp",EDGE,"E878"),sQuery(id+"F0.wireOp",EDGE,"E879"),sQuery(id+"F0.wireOp",EDGE,"E880"),sQuery(id+"F0.wireOp",EDGE,"E881"),sQuery(id+"F0.wireOp",EDGE,"E882"),sQuery(id+"F0.wireOp",EDGE,"E883"),sQuery(id+"F0.wireOp",EDGE,"E884"),sQuery(id+"F0.wireOp",EDGE,"E885"),sQuery(id+"F0.wireOp",EDGE,"E886"),sQuery(id+"F0.wireOp",EDGE,"E887"),sQuery(id+"F0.wireOp",EDGE,"E888"),sQuery(id+"F0.wireOp",EDGE,"E889"),sQuery(id+"F0.wireOp",EDGE,"E890"),sQuery(id+"F0.wireOp",EDGE,"E891"),sQuery(id+"F0.wireOp",EDGE,"E892"),sQuery(id+"F0.wireOp",EDGE,"E893"),sQuery(id+"F0.wireOp",EDGE,"E894"),sQuery(id+"F0.wireOp",EDGE,"E895"),sQuery(id+"F0.wireOp",EDGE,"E896"),sQuery(id+"F0.wireOp",EDGE,"E897"),sQuery(id+"F0.wireOp",EDGE,"E898"),sQuery(id+"F0.wireOp",EDGE,"E899"),sQuery(id+"F0.wireOp",EDGE,"E900"),sQuery(id+"F0.wireOp",EDGE,"E901"),sQuery(id+"F0.wireOp",EDGE,"E902"),sQuery(id+"F0.wireOp",EDGE,"E903"),sQuery(id+"F0.wireOp",EDGE,"E904"),sQuery(id+"F0.wireOp",EDGE,"E905"),sQuery(id+"F0.wireOp",EDGE,"E906"),sQuery(id+"F0.wireOp",EDGE,"E907"),sQuery(id+"F0.wireOp",EDGE,"E908"),sQuery(id+"F0.wireOp",EDGE,"E909"),sQuery(id+"F0.wireOp",EDGE,"E910"),sQuery(id+"F0.wireOp",EDGE,"E911"),sQuery(id+"F0.wireOp",EDGE,"E912"),sQuery(id+"F0.wireOp",EDGE,"E913"),sQuery(id+"F0.wireOp",EDGE,"E914"),sQuery(id+"F0.wireOp",EDGE,"E915"),sQuery(id+"F0.wireOp",EDGE,"E916"),sQuery(id+"F0.wireOp",EDGE,"E917"),sQuery(id+"F0.wireOp",EDGE,"E918"),sQuery(id+"F0.wireOp",EDGE,"E919"),sQuery(id+"F0.wireOp",EDGE,"E920"),sQuery(id+"F0.wireOp",EDGE,"E921"),sQuery(id+"F0.wireOp",EDGE,"E922"),sQuery(id+"F0.wireOp",EDGE,"E923"),sQuery(id+"F0.wireOp",EDGE,"E924"),sQuery(id+"F0.wireOp",EDGE,"E925"),sQuery(id+"F0.wireOp",EDGE,"E926"),sQuery(id+"F0.wireOp",EDGE,"E927"),sQuery(id+"F0.wireOp",EDGE,"E928"),sQuery(id+"F0.wireOp",EDGE,"E929"),sQuery(id+"F0.wireOp",EDGE,"E930"),sQuery(id+"F0.wireOp",EDGE,"E931"),sQuery(id+"F0.wireOp",EDGE,"E932"),sQuery(id+"F0.wireOp",EDGE,"E933"),sQuery(id+"F0.wireOp",EDGE,"E934"),sQuery(id+"F0.wireOp",EDGE,"E935"),sQuery(id+"F0.wireOp",EDGE,"E936"),sQuery(id+"F0.wireOp",EDGE,"E937"),sQuery(id+"F0.wireOp",EDGE,"E938"),sQuery(id+"F0.wireOp",EDGE,"E939"),sQuery(id+"F0.wireOp",EDGE,"E940"),sQuery(id+"F0.wireOp",EDGE,"E941"),sQuery(id+"F0.wireOp",EDGE,"E942"),sQuery(id+"F0.wireOp",EDGE,"E943"),sQuery(id+"F0.wireOp",EDGE,"E944"),sQuery(id+"F0.wireOp",EDGE,"E945"),sQuery(id+"F0.wireOp",EDGE,"E946"),sQuery(id+"F0.wireOp",EDGE,"E947"),sQuery(id+"F0.wireOp",EDGE,"E948"),sQuery(id+"F0.wireOp",EDGE,"E949"),sQuery(id+"F0.wireOp",EDGE,"E950"),sQuery(id+"F0.wireOp",EDGE,"E951"),sQuery(id+"F0.wireOp",EDGE,"E952"),sQuery(id+"F0.wireOp",EDGE,"E953"),sQuery(id+"F0.wireOp",EDGE,"E954"),sQuery(id+"F0.wireOp",EDGE,"E955"),sQuery(id+"F0.wireOp",EDGE,"E956"),sQuery(id+"F0.wireOp",EDGE,"E957"),sQuery(id+"F0.wireOp",EDGE,"E958"),sQuery(id+"F0.wireOp",EDGE,"E959"),sQuery(id+"F0.wireOp",EDGE,"E960"),sQuery(id+"F0.wireOp",EDGE,"E961"),sQuery(id+"F0.wireOp",EDGE,"E962"),sQuery(id+"F0.wireOp",EDGE,"E963")])],"isStart":false});
            var sketch = newSketch(context, id + "F2", { "sketchPlane" : qUnion([Q0])});
            skLineSegment(sketch, "E1208.0", {"start": v(228.6, 87.97) * mm, "end": v(228.6, 99.82) * mm});
            skLineSegment(sketch, "E1209.0", {"start": v(-228.6, 99.82) * mm, "end": v(-228.6, 111.68) * mm});
            skLineSegment(sketch, "E1210.0", {"start": v(-228.6, 76.12) * mm, "end": v(-228.6, 87.97) * mm});
            skLineSegment(sketch, "E1211", {"start": v(-228.6, 99.82) * mm, "end": v(-228.6, 87.97) * mm});
            skLineSegment(sketch, "E1212", {"start": v(228.6, 93.9) * mm, "end": v(-228.6, 93.9) * mm, "construction": true});
            skCircle(sketch, "E1213", {"center": v(-172.49, 93.9) * mm, "radius": 30.16 * mm});
            skCircle(sketch, "E1214", {"center": v(163.83, 93.9) * mm, "radius": 30.16 * mm});
            skLineSegment(sketch, "E1215.0", {"start": v(-18.54, -5) * mm, "end": v(-6.18, -5) * mm});
            skLineSegment(sketch, "E1216.0", {"start": v(-30.89, -305.04) * mm, "end": v(-18.54, -305.04) * mm});
            skSolve(sketch);
        }
        {
            var Q0;
            Q0=makeQuery(id+"F2.imprint","IMPRINT",FACE,{"disambiguationData":[TD([[makeQuery(id+"F2.imprint","IMPRINT",EDGE,{"derivedFrom":sQuery(id+"F2.wireOp",EDGE,"E1213")}),1.0]])]});
            var Q1;
            Q1=makeQuery(id+"F2.imprint","IMPRINT",FACE,{"disambiguationData":[TD([[makeQuery(id+"F2.imprint","IMPRINT",EDGE,{"derivedFrom":sQuery(id+"F2.wireOp",EDGE,"E1214")}),1.0]])]});
            extrude(context, id + "F3", {"entities" : qUnion([Q0, Q1]), "operationType" : NewBodyOperationType.REMOVE, "oppositeDirection" : true, "depth" : 25.4 * mm});
        }
        {
            var Q0;
            Q0=makeQuery(id+"F1.opExtrude","CAP_FACE",FACE,{"disambiguationData":[OSD([sQuery(id+"F0.wireOp",EDGE,"E0"),sQuery(id+"F0.wireOp",EDGE,"E1"),sQuery(id+"F0.wireOp",EDGE,"E2"),sQuery(id+"F0.wireOp",EDGE,"E3"),sQuery(id+"F0.wireOp",EDGE,"E4"),sQuery(id+"F0.wireOp",EDGE,"E5"),sQuery(id+"F0.wireOp",EDGE,"E6"),sQuery(id+"F0.wireOp",EDGE,"E7"),sQuery(id+"F0.wireOp",EDGE,"E8"),sQuery(id+"F0.wireOp",EDGE,"E9"),sQuery(id+"F0.wireOp",EDGE,"E10"),sQuery(id+"F0.wireOp",EDGE,"E11"),sQuery(id+"F0.wireOp",EDGE,"E12"),sQuery(id+"F0.wireOp",EDGE,"E13"),sQuery(id+"F0.wireOp",EDGE,"E14"),sQuery(id+"F0.wireOp",EDGE,"E15"),sQuery(id+"F0.wireOp",EDGE,"E16"),sQuery(id+"F0.wireOp",EDGE,"E17"),sQuery(id+"F0.wireOp",EDGE,"E18"),sQuery(id+"F0.wireOp",EDGE,"E19"),sQuery(id+"F0.wireOp",EDGE,"E20"),sQuery(id+"F0.wireOp",EDGE,"E21"),sQuery(id+"F0.wireOp",EDGE,"E22"),sQuery(id+"F0.wireOp",EDGE,"E23"),sQuery(id+"F0.wireOp",EDGE,"E24"),sQuery(id+"F0.wireOp",EDGE,"E25"),sQuery(id+"F0.wireOp",EDGE,"E26"),sQuery(id+"F0.wireOp",EDGE,"E27"),sQuery(id+"F0.wireOp",EDGE,"E28"),sQuery(id+"F0.wireOp",EDGE,"E29"),sQuery(id+"F0.wireOp",EDGE,"E30"),sQuery(id+"F0.wireOp",EDGE,"E31"),sQuery(id+"F0.wireOp",EDGE,"E32"),sQuery(id+"F0.wireOp",EDGE,"E33"),sQuery(id+"F0.wireOp",EDGE,"E34"),sQuery(id+"F0.wireOp",EDGE,"E35"),sQuery(id+"F0.wireOp",EDGE,"E36"),sQuery(id+"F0.wireOp",EDGE,"E37"),sQuery(id+"F0.wireOp",EDGE,"E38"),sQuery(id+"F0.wireOp",EDGE,"E39"),sQuery(id+"F0.wireOp",EDGE,"E40"),sQuery(id+"F0.wireOp",EDGE,"E41"),sQuery(id+"F0.wireOp",EDGE,"E42"),sQuery(id+"F0.wireOp",EDGE,"E43"),sQuery(id+"F0.wireOp",EDGE,"E44"),sQuery(id+"F0.wireOp",EDGE,"E45"),sQuery(id+"F0.wireOp",EDGE,"E46"),sQuery(id+"F0.wireOp",EDGE,"E47"),sQuery(id+"F0.wireOp",EDGE,"E48"),sQuery(id+"F0.wireOp",EDGE,"E49"),sQuery(id+"F0.wireOp",EDGE,"E50"),sQuery(id+"F0.wireOp",EDGE,"E51"),sQuery(id+"F0.wireOp",EDGE,"E52"),sQuery(id+"F0.wireOp",EDGE,"E53"),sQuery(id+"F0.wireOp",EDGE,"E54"),sQuery(id+"F0.wireOp",EDGE,"E55"),sQuery(id+"F0.wireOp",EDGE,"E56"),sQuery(id+"F0.wireOp",EDGE,"E57"),sQuery(id+"F0.wireOp",EDGE,"E58"),sQuery(id+"F0.wireOp",EDGE,"E59"),sQuery(id+"F0.wireOp",EDGE,"E60"),sQuery(id+"F0.wireOp",EDGE,"E61"),sQuery(id+"F0.wireOp",EDGE,"E62"),sQuery(id+"F0.wireOp",EDGE,"E63"),sQuery(id+"F0.wireOp",EDGE,"E64"),sQuery(id+"F0.wireOp",EDGE,"E65"),sQuery(id+"F0.wireOp",EDGE,"E66"),sQuery(id+"F0.wireOp",EDGE,"E67"),sQuery(id+"F0.wireOp",EDGE,"E68"),sQuery(id+"F0.wireOp",EDGE,"E69"),sQuery(id+"F0.wireOp",EDGE,"E70"),sQuery(id+"F0.wireOp",EDGE,"E71"),sQuery(id+"F0.wireOp",EDGE,"E72"),sQuery(id+"F0.wireOp",EDGE,"E73"),sQuery(id+"F0.wireOp",EDGE,"E74"),sQuery(id+"F0.wireOp",EDGE,"E75"),sQuery(id+"F0.wireOp",EDGE,"E76"),sQuery(id+"F0.wireOp",EDGE,"E77"),sQuery(id+"F0.wireOp",EDGE,"E78"),sQuery(id+"F0.wireOp",EDGE,"E79"),sQuery(id+"F0.wireOp",EDGE,"E80"),sQuery(id+"F0.wireOp",EDGE,"E81"),sQuery(id+"F0.wireOp",EDGE,"E82"),sQuery(id+"F0.wireOp",EDGE,"E83"),sQuery(id+"F0.wireOp",EDGE,"E84"),sQuery(id+"F0.wireOp",EDGE,"E85"),sQuery(id+"F0.wireOp",EDGE,"E86"),sQuery(id+"F0.wireOp",EDGE,"E87"),sQuery(id+"F0.wireOp",EDGE,"E88"),sQuery(id+"F0.wireOp",EDGE,"E89"),sQuery(id+"F0.wireOp",EDGE,"E90"),sQuery(id+"F0.wireOp",EDGE,"E91"),sQuery(id+"F0.wireOp",EDGE,"E92"),sQuery(id+"F0.wireOp",EDGE,"E93"),sQuery(id+"F0.wireOp",EDGE,"E94"),sQuery(id+"F0.wireOp",EDGE,"E95"),sQuery(id+"F0.wireOp",EDGE,"E96"),sQuery(id+"F0.wireOp",EDGE,"E97"),sQuery(id+"F0.wireOp",EDGE,"E98"),sQuery(id+"F0.wireOp",EDGE,"E99"),sQuery(id+"F0.wireOp",EDGE,"E100"),sQuery(id+"F0.wireOp",EDGE,"E101"),sQuery(id+"F0.wireOp",EDGE,"E102"),sQuery(id+"F0.wireOp",EDGE,"E103"),sQuery(id+"F0.wireOp",EDGE,"E104"),sQuery(id+"F0.wireOp",EDGE,"E105"),sQuery(id+"F0.wireOp",EDGE,"E106"),sQuery(id+"F0.wireOp",EDGE,"E107"),sQuery(id+"F0.wireOp",EDGE,"E108"),sQuery(id+"F0.wireOp",EDGE,"E109"),sQuery(id+"F0.wireOp",EDGE,"E110"),sQuery(id+"F0.wireOp",EDGE,"E111"),sQuery(id+"F0.wireOp",EDGE,"E112"),sQuery(id+"F0.wireOp",EDGE,"E113"),sQuery(id+"F0.wireOp",EDGE,"E114"),sQuery(id+"F0.wireOp",EDGE,"E115"),sQuery(id+"F0.wireOp",EDGE,"E116"),sQuery(id+"F0.wireOp",EDGE,"E117"),sQuery(id+"F0.wireOp",EDGE,"E118"),sQuery(id+"F0.wireOp",EDGE,"E119"),sQuery(id+"F0.wireOp",EDGE,"E120"),sQuery(id+"F0.wireOp",EDGE,"E121"),sQuery(id+"F0.wireOp",EDGE,"E122"),sQuery(id+"F0.wireOp",EDGE,"E123"),sQuery(id+"F0.wireOp",EDGE,"E124"),sQuery(id+"F0.wireOp",EDGE,"E125"),sQuery(id+"F0.wireOp",EDGE,"E126"),sQuery(id+"F0.wireOp",EDGE,"E127"),sQuery(id+"F0.wireOp",EDGE,"E128"),sQuery(id+"F0.wireOp",EDGE,"E129"),sQuery(id+"F0.wireOp",EDGE,"E130"),sQuery(id+"F0.wireOp",EDGE,"E131"),sQuery(id+"F0.wireOp",EDGE,"E132"),sQuery(id+"F0.wireOp",EDGE,"E133"),sQuery(id+"F0.wireOp",EDGE,"E134"),sQuery(id+"F0.wireOp",EDGE,"E135"),sQuery(id+"F0.wireOp",EDGE,"E136"),sQuery(id+"F0.wireOp",EDGE,"E137"),sQuery(id+"F0.wireOp",EDGE,"E138"),sQuery(id+"F0.wireOp",EDGE,"E139"),sQuery(id+"F0.wireOp",EDGE,"E140"),sQuery(id+"F0.wireOp",EDGE,"E141"),sQuery(id+"F0.wireOp",EDGE,"E142"),sQuery(id+"F0.wireOp",EDGE,"E143"),sQuery(id+"F0.wireOp",EDGE,"E144"),sQuery(id+"F0.wireOp",EDGE,"E145"),sQuery(id+"F0.wireOp",EDGE,"E146"),sQuery(id+"F0.wireOp",EDGE,"E147"),sQuery(id+"F0.wireOp",EDGE,"E148"),sQuery(id+"F0.wireOp",EDGE,"E149"),sQuery(id+"F0.wireOp",EDGE,"E150"),sQuery(id+"F0.wireOp",EDGE,"E151"),sQuery(id+"F0.wireOp",EDGE,"E152"),sQuery(id+"F0.wireOp",EDGE,"E153"),sQuery(id+"F0.wireOp",EDGE,"E154"),sQuery(id+"F0.wireOp",EDGE,"E155"),sQuery(id+"F0.wireOp",EDGE,"E156"),sQuery(id+"F0.wireOp",EDGE,"E157"),sQuery(id+"F0.wireOp",EDGE,"E158"),sQuery(id+"F0.wireOp",EDGE,"E159"),sQuery(id+"F0.wireOp",EDGE,"E160"),sQuery(id+"F0.wireOp",EDGE,"E161"),sQuery(id+"F0.wireOp",EDGE,"E162"),sQuery(id+"F0.wireOp",EDGE,"E163"),sQuery(id+"F0.wireOp",EDGE,"E164"),sQuery(id+"F0.wireOp",EDGE,"E165"),sQuery(id+"F0.wireOp",EDGE,"E166"),sQuery(id+"F0.wireOp",EDGE,"E167"),sQuery(id+"F0.wireOp",EDGE,"E168"),sQuery(id+"F0.wireOp",EDGE,"E169"),sQuery(id+"F0.wireOp",EDGE,"E170"),sQuery(id+"F0.wireOp",EDGE,"E171"),sQuery(id+"F0.wireOp",EDGE,"E172"),sQuery(id+"F0.wireOp",EDGE,"E173"),sQuery(id+"F0.wireOp",EDGE,"E174"),sQuery(id+"F0.wireOp",EDGE,"E175"),sQuery(id+"F0.wireOp",EDGE,"E176"),sQuery(id+"F0.wireOp",EDGE,"E177"),sQuery(id+"F0.wireOp",EDGE,"E178"),sQuery(id+"F0.wireOp",EDGE,"E179"),sQuery(id+"F0.wireOp",EDGE,"E180"),sQuery(id+"F0.wireOp",EDGE,"E181"),sQuery(id+"F0.wireOp",EDGE,"E182"),sQuery(id+"F0.wireOp",EDGE,"E183"),sQuery(id+"F0.wireOp",EDGE,"E184"),sQuery(id+"F0.wireOp",EDGE,"E185"),sQuery(id+"F0.wireOp",EDGE,"E186"),sQuery(id+"F0.wireOp",EDGE,"E187"),sQuery(id+"F0.wireOp",EDGE,"E188"),sQuery(id+"F0.wireOp",EDGE,"E189"),sQuery(id+"F0.wireOp",EDGE,"E190"),sQuery(id+"F0.wireOp",EDGE,"E191"),sQuery(id+"F0.wireOp",EDGE,"E192"),sQuery(id+"F0.wireOp",EDGE,"E193"),sQuery(id+"F0.wireOp",EDGE,"E194"),sQuery(id+"F0.wireOp",EDGE,"E195"),sQuery(id+"F0.wireOp",EDGE,"E196"),sQuery(id+"F0.wireOp",EDGE,"E197"),sQuery(id+"F0.wireOp",EDGE,"E198"),sQuery(id+"F0.wireOp",EDGE,"E199"),sQuery(id+"F0.wireOp",EDGE,"E200"),sQuery(id+"F0.wireOp",EDGE,"E201"),sQuery(id+"F0.wireOp",EDGE,"E202"),sQuery(id+"F0.wireOp",EDGE,"E203")])],"isStart":false});
            var sketch = newSketch(context, id + "F4", { "sketchPlane" : qUnion([Q0])});
            skLineSegment(sketch, "E1217.0", {"start": v(-228.6, -402.78) * mm, "end": v(-228.6, -390.92) * mm});
            skLineSegment(sketch, "E1218.0", {"start": v(-228.6, -426.48) * mm, "end": v(-228.6, -414.63) * mm});
            skLineSegment(sketch, "E1219", {"start": v(-228.6, -402.78) * mm, "end": v(-228.6, -414.63) * mm});
            skLineSegment(sketch, "E1220.0", {"start": v(228.6, -414.63) * mm, "end": v(228.6, -402.78) * mm});
            skLineSegment(sketch, "E1221", {"start": v(-228.6, -408.7) * mm, "end": v(228.6, -408.7) * mm, "construction": true});
            skCircle(sketch, "E1222", {"center": v(-169.2, -408.7) * mm, "radius": 30.16 * mm});
            skCircle(sketch, "E1223", {"center": v(167.13, -408.7) * mm, "radius": 30.16 * mm});
            skSolve(sketch);
        }
        {
            var Q0;
            Q0 = qSketchRegion(id + "F4", true);
            extrude(context, id + "F5", {"entities" : qUnion([Q0]), "operationType" : NewBodyOperationType.REMOVE, "oppositeDirection" : true, "depth" : 314.96 * mm});
        }
    });
